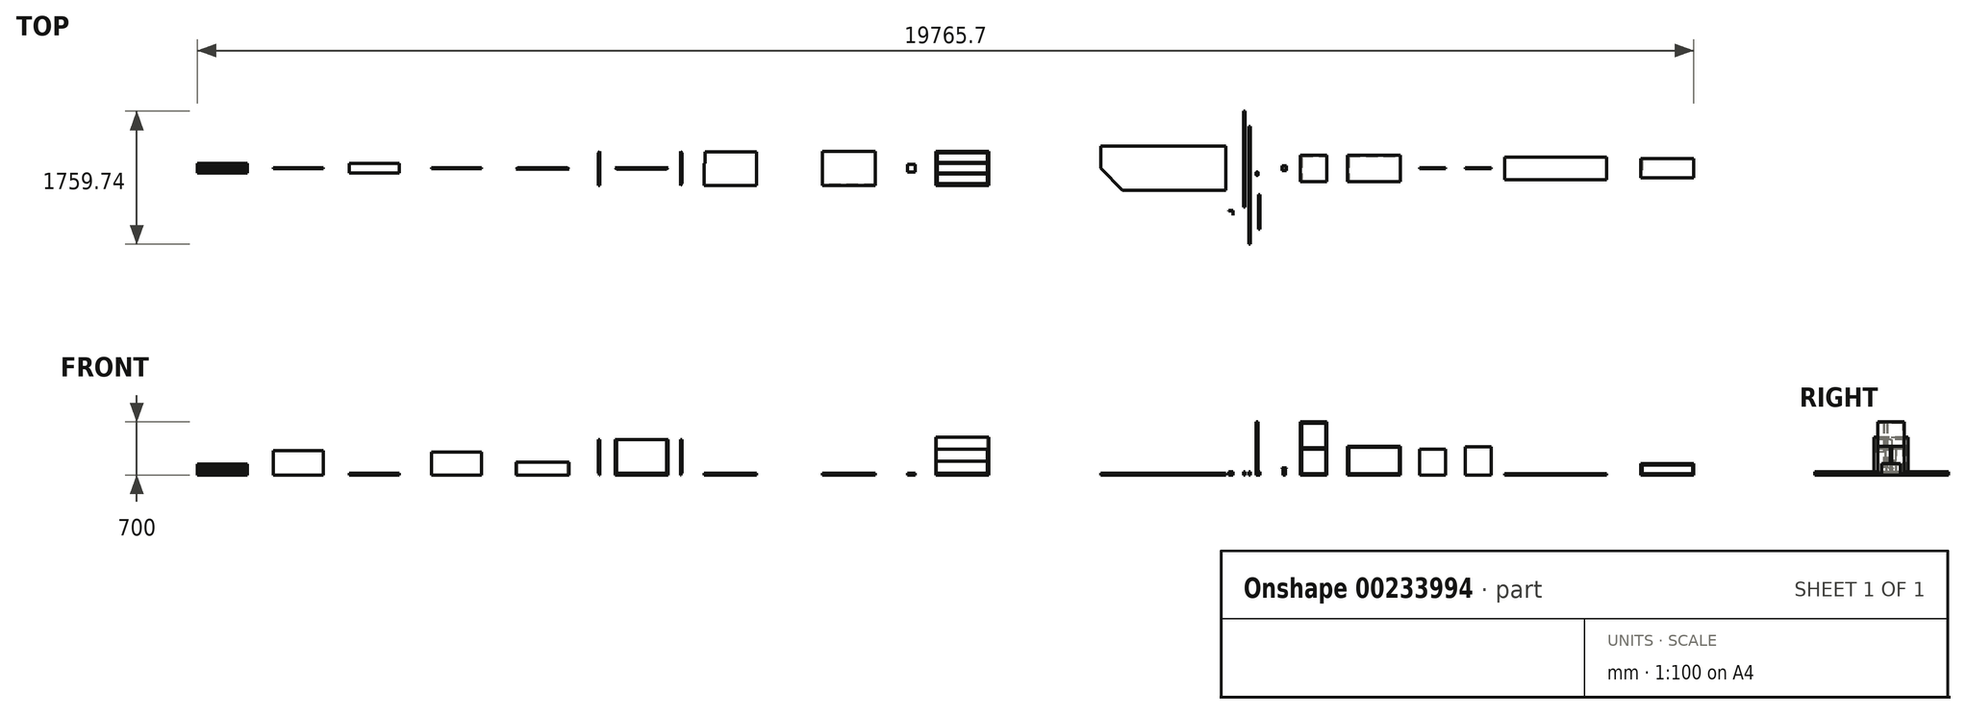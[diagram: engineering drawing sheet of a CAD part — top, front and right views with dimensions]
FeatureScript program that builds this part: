
annotation { "Feature Type Name" : "Feature", "Feature Type Description" : "" }
export const myFeature = defineFeature(function(context is Context, id is Id, definition is map)
    precondition{}
    {
        {
            var Q0;
            Q0=qCreatedBy(makeId("Top.planeOp"),FACE);
            var sketch = newSketch(context, id + "F0", { "sketchPlane" : qUnion([Q0])});
            skLineSegment(sketch, "E0.bottom", {"start": v(-825, -290) * mm, "end": v(825, -290) * mm});
            skLineSegment(sketch, "E0.top", {"start": v(-825, 290) * mm, "end": v(825, 290) * mm});
            skLineSegment(sketch, "E0.left", {"start": v(-825, -290) * mm, "end": v(-825, 290) * mm});
            skLineSegment(sketch, "E0.right", {"start": v(825, -290) * mm, "end": v(825, 290) * mm});
            skPoint(sketch, "E0.middle", {"position": v(0, 0) * mm});
            skSolve(sketch);
        }
        {
            var Q0;
            Q0 = qSketchRegion(id + "F0", true);
            extrude(context, id + "F1", {"entities" : qUnion([Q0]), "depth" : 21 * mm});
        }
        {
            var Q0;
            Q0=qCreatedBy(makeId("Top.planeOp"),FACE);
            var sketch = newSketch(context, id + "F2", { "sketchPlane" : qUnion([Q0])});
            skLineSegment(sketch, "E1.bottom", {"start": v(1133.64, 555.5) * mm, "end": v(1151.64, 555.5) * mm});
            skLineSegment(sketch, "E1.top", {"start": v(1133.64, -1004.5) * mm, "end": v(1151.64, -1004.5) * mm});
            skLineSegment(sketch, "E1.left", {"start": v(1133.64, 555.5) * mm, "end": v(1133.64, -1004.5) * mm});
            skLineSegment(sketch, "E1.right", {"start": v(1151.64, 555.5) * mm, "end": v(1151.64, -1004.5) * mm});
            skSolve(sketch);
        }
        {
            var Q0;
            Q0 = qSketchRegion(id + "F2", true);
            extrude(context, id + "F3", {"entities" : qUnion([Q0]), "depth" : 40 * mm});
        }
        {
            var Q0;
            Q0=qCreatedBy(makeId("Top.planeOp"),FACE);
            var sketch = newSketch(context, id + "F4", { "sketchPlane" : qUnion([Q0])});
            skLineSegment(sketch, "E2.bottom", {"start": v(1258.17, -803.03) * mm, "end": v(1276.17, -803.03) * mm});
            skLineSegment(sketch, "E2.top", {"start": v(1258.17, -351.03) * mm, "end": v(1276.17, -351.03) * mm});
            skLineSegment(sketch, "E2.left", {"start": v(1258.17, -803.03) * mm, "end": v(1258.17, -351.03) * mm});
            skLineSegment(sketch, "E2.right", {"start": v(1276.17, -803.03) * mm, "end": v(1276.17, -351.03) * mm});
            skSolve(sketch);
        }
        {
            var Q0;
            Q0 = qSketchRegion(id + "F4", true);
            extrude(context, id + "F5", {"entities" : qUnion([Q0]), "depth" : 40 * mm});
        }
        {
            var Q0;
            Q0=qCreatedBy(makeId("Top.planeOp"),FACE);
            var sketch = newSketch(context, id + "F6", { "sketchPlane" : qUnion([Q0])});
            skLineSegment(sketch, "E3", {"start": v(923.66, -561.71) * mm, "end": v(863.66, -561.71) * mm});
            skLineSegment(sketch, "E4", {"start": v(863.66, -561.71) * mm, "end": v(863.66, -559.71) * mm});
            skLineSegment(sketch, "E5", {"start": v(863.66, -559.71) * mm, "end": v(925.66, -559.71) * mm});
            skLineSegment(sketch, "E6", {"start": v(925.66, -559.71) * mm, "end": v(925.66, -621.71) * mm});
            skLineSegment(sketch, "E7", {"start": v(925.66, -621.71) * mm, "end": v(923.66, -621.71) * mm});
            skLineSegment(sketch, "E8", {"start": v(923.66, -621.71) * mm, "end": v(923.66, -561.71) * mm});
            skSolve(sketch);
        }
        {
            var Q0;
            Q0 = qSketchRegion(id + "F6", true);
            extrude(context, id + "F7", {"entities" : qUnion([Q0]), "depth" : 40 * mm});
        }
        {
            var Q0;
            Q0=qCreatedBy(makeId("Top.planeOp"),FACE);
            var sketch = newSketch(context, id + "F8", { "sketchPlane" : qUnion([Q0])});
            skLineSegment(sketch, "E9", {"start": v(1228.45, -53.77) * mm, "end": v(1228.45, -90.77) * mm});
            skArc(sketch, "E10", {"start": v(1256.45, -53.77) * mm, "mid": v(1242.45, -48.05) * mm, "end": v(1228.45, -53.77) * mm});
            skLineSegment(sketch, "E11", {"start": v(1256.45, -53.77) * mm, "end": v(1256.45, -90.77) * mm});
            skArc(sketch, "E12", {"start": v(1228.45, -90.77) * mm, "mid": v(1242.45, -96.48) * mm, "end": v(1256.45, -90.77) * mm});
            skSolve(sketch);
        }
        {
            var Q0;
            Q0 = qSketchRegion(id + "F8", true);
            extrude(context, id + "F9", {"entities" : qUnion([Q0]), "depth" : 700 * mm});
        }
        {
            var Q0;
            Q0=makeQuery(id+"F1.opExtrude","CAP_FACE",FACE,{"disambiguationData":[OSD([sQuery(id+"F0.wireOp",EDGE,"E0.bottom"),sQuery(id+"F0.wireOp",EDGE,"E0.top"),sQuery(id+"F0.wireOp",EDGE,"E0.left"),sQuery(id+"F0.wireOp",EDGE,"E0.right")])],"isStart":false});
            var sketch = newSketch(context, id + "F10", { "sketchPlane" : qUnion([Q0])});
            skLineSegment(sketch, "E13", {"start": v(-825, 0) * mm, "end": v(-535, -290) * mm});
            skLineSegment(sketch, "E14", {"start": v(-535, -290) * mm, "end": v(-825, -290) * mm});
            skLineSegment(sketch, "E15", {"start": v(-825, -290) * mm, "end": v(-825, 0) * mm});
            skSolve(sketch);
        }
        {
            var Q0;
            Q0 = qSketchRegion(id + "F10", true);
            extrude(context, id + "F11", {"entities" : qUnion([Q0]), "operationType" : NewBodyOperationType.REMOVE, "endBound" : BoundingType.UP_TO_NEXT, "oppositeDirection" : true, "depth" : 25 * mm});
        }
        {
            var Q0;
            Q0=qCreatedBy(makeId("Top.planeOp"),FACE);
            var sketch = newSketch(context, id + "F12", { "sketchPlane" : qUnion([Q0])});
            skLineSegment(sketch, "E16", {"start": v(1082.97, 755.24) * mm, "end": v(1064.97, 755.24) * mm});
            skLineSegment(sketch, "E17", {"start": v(1064.97, 755.24) * mm, "end": v(1064.97, -514.76) * mm});
            skLineSegment(sketch, "E18", {"start": v(1064.97, -514.76) * mm, "end": v(1082.97, -514.76) * mm});
            skLineSegment(sketch, "E19", {"start": v(1082.97, -514.76) * mm, "end": v(1082.97, 755.24) * mm});
            skSolve(sketch);
        }
        {
            var Q0;
            Q0 = qSketchRegion(id + "F12", true);
            extrude(context, id + "F13", {"entities" : qUnion([Q0]), "depth" : 40 * mm});
        }
        {
            var Q0;
            Q0=qCreatedBy(makeId("Top.planeOp"),FACE);
            var sketch = newSketch(context, id + "F14", { "sketchPlane" : qUnion([Q0])});
            skLineSegment(sketch, "E20.bottom", {"start": v(1813.46, -175) * mm, "end": v(2163.46, -175) * mm});
            skLineSegment(sketch, "E20.top", {"start": v(1813.46, 175) * mm, "end": v(2163.46, 175) * mm});
            skLineSegment(sketch, "E20.left", {"start": v(1813.46, -175) * mm, "end": v(1813.46, 175) * mm});
            skLineSegment(sketch, "E20.right", {"start": v(2163.46, -175) * mm, "end": v(2163.46, 175) * mm});
            skPoint(sketch, "E20.middle", {"position": v(1988.46, 0) * mm});
            skSolve(sketch);
        }
        {
            var Q0;
            Q0 = qSketchRegion(id + "F14", true);
            extrude(context, id + "F15", {"entities" : qUnion([Q0]), "depth" : 700 * mm});
        }
        {
            var Q0;
            Q0=makeQuery(id+"F15.opExtrude","SWEPT_FACE",FACE,{"disambiguationData":[OSD([sQuery(id+"F14.wireOp",EDGE,"E20.bottom")])]});
            var sketch = newSketch(context, id + "F16", { "sketchPlane" : qUnion([Q0])});
            skLineSegment(sketch, "E21.bottom", {"start": v(1829.46, 358) * mm, "end": v(2147.46, 358) * mm});
            skLineSegment(sketch, "E21.top", {"start": v(1829.46, 684) * mm, "end": v(2147.46, 684) * mm});
            skLineSegment(sketch, "E21.left", {"start": v(1829.46, 358) * mm, "end": v(1829.46, 684) * mm});
            skLineSegment(sketch, "E21.right", {"start": v(2147.46, 358) * mm, "end": v(2147.46, 684) * mm});
            skPoint(sketch, "E21.middle", {"position": v(1988.46, 521) * mm});
            skPoint(sketch, "E21.middle.positionSnap0", {"position": v(1988.46, 700) * mm});
            skPoint(sketch, "E21.centerSnap0", {"position": v(1988.46, 700) * mm});
            skLineSegment(sketch, "E22.bottom", {"start": v(1829.46, 16) * mm, "end": v(2147.46, 16) * mm});
            skLineSegment(sketch, "E22.top", {"start": v(1829.46, 342) * mm, "end": v(2147.46, 342) * mm});
            skLineSegment(sketch, "E22.left", {"start": v(1829.46, 16) * mm, "end": v(1829.46, 342) * mm});
            skLineSegment(sketch, "E22.right", {"start": v(2147.46, 16) * mm, "end": v(2147.46, 342) * mm});
            skPoint(sketch, "E22.middle", {"position": v(1988.46, 179) * mm});
            skSolve(sketch);
        }
        {
            var Q0;
            Q0 = qSketchRegion(id + "F16", true);
            extrude(context, id + "F17", {"entities" : qUnion([Q0]), "operationType" : NewBodyOperationType.REMOVE, "oppositeDirection" : true, "depth" : 334 * mm});
        }
        {
            var Q0;
            Q0=qCreatedBy(makeId("Top.planeOp"),FACE);
            var sketch = newSketch(context, id + "F18", { "sketchPlane" : qUnion([Q0])});
            skLineSegment(sketch, "E23.bottom", {"start": v(2436.18, -175) * mm, "end": v(3136.18, -175) * mm});
            skLineSegment(sketch, "E23.top", {"start": v(2436.18, 175) * mm, "end": v(3136.18, 175) * mm});
            skLineSegment(sketch, "E23.left", {"start": v(2436.18, -175) * mm, "end": v(2436.18, 175) * mm});
            skLineSegment(sketch, "E23.right", {"start": v(3136.18, -175) * mm, "end": v(3136.18, 175) * mm});
            skPoint(sketch, "E23.middle", {"position": v(2786.18, 0) * mm});
            skSolve(sketch);
        }
        {
            var Q0;
            Q0 = qSketchRegion(id + "F18", true);
            extrude(context, id + "F19", {"entities" : qUnion([Q0]), "depth" : 380 * mm});
        }
        {
            var Q0;
            Q0=makeQuery(id+"F19.opExtrude","SWEPT_FACE",FACE,{"disambiguationData":[OSD([sQuery(id+"F18.wireOp",EDGE,"E23.bottom")])]});
            var sketch = newSketch(context, id + "F20", { "sketchPlane" : qUnion([Q0])});
            skLineSegment(sketch, "E24.bottom", {"start": v(2452.18, 16) * mm, "end": v(3120.18, 16) * mm});
            skLineSegment(sketch, "E24.top", {"start": v(2452.18, 364) * mm, "end": v(3120.18, 364) * mm});
            skLineSegment(sketch, "E24.left", {"start": v(2452.18, 16) * mm, "end": v(2452.18, 364) * mm});
            skLineSegment(sketch, "E24.right", {"start": v(3120.18, 16) * mm, "end": v(3120.18, 364) * mm});
            skPoint(sketch, "E24.middle", {"position": v(2786.18, 190) * mm});
            skPoint(sketch, "E24.middle.positionSnap0", {"position": v(2436.18, 190) * mm});
            skPoint(sketch, "E24.centerSnap0", {"position": v(2436.18, 190) * mm});
            skSolve(sketch);
        }
        {
            var Q0;
            Q0 = qSketchRegion(id + "F20", true);
            extrude(context, id + "F21", {"entities" : qUnion([Q0]), "operationType" : NewBodyOperationType.REMOVE, "oppositeDirection" : true, "depth" : 334 * mm});
        }
        {
            var Q0;
            Q0=qCreatedBy(makeId("Top.planeOp"),FACE);
            var sketch = newSketch(context, id + "F22", { "sketchPlane" : qUnion([Q0])});
            skLineSegment(sketch, "E25.bottom", {"start": v(3728.23, -8) * mm, "end": v(3388.23, -8) * mm});
            skLineSegment(sketch, "E25.top", {"start": v(3728.23, 8) * mm, "end": v(3388.23, 8) * mm});
            skLineSegment(sketch, "E25.left", {"start": v(3728.23, -8) * mm, "end": v(3728.23, 8) * mm});
            skLineSegment(sketch, "E25.right", {"start": v(3388.23, -8) * mm, "end": v(3388.23, 8) * mm});
            skPoint(sketch, "E25.middle", {"position": v(3558.23, 0) * mm});
            skSolve(sketch);
        }
        {
            var Q0;
            Q0 = qSketchRegion(id + "F22", true);
            extrude(context, id + "F23", {"entities" : qUnion([Q0]), "depth" : 340 * mm});
        }
        {
            var Q0;
            Q0=qCreatedBy(makeId("Top.planeOp"),FACE);
            var sketch = newSketch(context, id + "F24", { "sketchPlane" : qUnion([Q0])});
            skLineSegment(sketch, "E26.bottom", {"start": v(3990.26, -8) * mm, "end": v(4330.26, -8) * mm});
            skLineSegment(sketch, "E26.top", {"start": v(3990.26, 8) * mm, "end": v(4330.26, 8) * mm});
            skLineSegment(sketch, "E26.left", {"start": v(3990.26, -8) * mm, "end": v(3990.26, 8) * mm});
            skLineSegment(sketch, "E26.right", {"start": v(4330.26, -8) * mm, "end": v(4330.26, 8) * mm});
            skPoint(sketch, "E26.middle", {"position": v(4160.26, 0) * mm});
            skSolve(sketch);
        }
        {
            var Q0;
            Q0 = qSketchRegion(id + "F24", true);
            extrude(context, id + "F25", {"entities" : qUnion([Q0]), "depth" : 370 * mm});
        }
        {
            var Q0;
            Q0=qCreatedBy(makeId("Top.planeOp"),FACE);
            var sketch = newSketch(context, id + "F26", { "sketchPlane" : qUnion([Q0])});
            skLineSegment(sketch, "E27.bottom", {"start": v(4509.18, -150) * mm, "end": v(5859.18, -150) * mm});
            skLineSegment(sketch, "E27.top", {"start": v(4509.18, 150) * mm, "end": v(5859.18, 150) * mm});
            skLineSegment(sketch, "E27.left", {"start": v(4509.18, -150) * mm, "end": v(4509.18, 150) * mm});
            skLineSegment(sketch, "E27.right", {"start": v(5859.18, -150) * mm, "end": v(5859.18, 150) * mm});
            skPoint(sketch, "E27.middle", {"position": v(5184.18, 0) * mm});
            skSolve(sketch);
        }
        {
            var Q0;
            Q0 = qSketchRegion(id + "F26", true);
            extrude(context, id + "F27", {"entities" : qUnion([Q0]), "depth" : 16 * mm});
        }
        {
            var Q0;
            Q0=qCreatedBy(makeId("Top.planeOp"),FACE);
            var sketch = newSketch(context, id + "F28", { "sketchPlane" : qUnion([Q0])});
            skLineSegment(sketch, "E28.bottom", {"start": v(1570, -30) * mm, "end": v(1630, -30) * mm});
            skLineSegment(sketch, "E28.top", {"start": v(1570, 30) * mm, "end": v(1630, 30) * mm});
            skLineSegment(sketch, "E28.left", {"start": v(1570, -30) * mm, "end": v(1570, 30) * mm});
            skLineSegment(sketch, "E28.right", {"start": v(1630, -30) * mm, "end": v(1630, 30) * mm});
            skPoint(sketch, "E28.middle", {"position": v(1600, 0) * mm});
            skSolve(sketch);
        }
        {
            var Q0;
            Q0 = qSketchRegion(id + "F28", true);
            extrude(context, id + "F29", {"entities" : qUnion([Q0]), "depth" : 90 * mm});
        }
        {
            var Q0;
            Q0=qCreatedBy(makeId("Front.planeOp"),FACE);
            var sketch = newSketch(context, id + "F30", { "sketchPlane" : qUnion([Q0])});
            skLineSegment(sketch, "E29", {"start": v(1600, 158.23) * mm, "end": v(1600, -41.77) * mm, "construction": true});
            skSolve(sketch);
        }
        {
            var Q0;
            Q0=qCreatedBy(makeId("Front.planeOp"),FACE);
            var sketch = newSketch(context, id + "F31", { "sketchPlane" : qUnion([Q0])});
            skLineSegment(sketch, "E30", {"start": v(1615, 0) * mm, "end": v(1615, 83) * mm});
            skLineSegment(sketch, "E31", {"start": v(1630, 85) * mm, "end": v(1620, 85) * mm});
            skLineSegment(sketch, "E32", {"start": v(1620, 85) * mm, "end": v(1615, 83) * mm});
            skLineSegment(sketch, "E33", {"start": v(1615, 0) * mm, "end": v(1649.67, 0) * mm});
            skLineSegment(sketch, "E34", {"start": v(1649.67, 0) * mm, "end": v(1649.67, 85) * mm});
            skLineSegment(sketch, "E35", {"start": v(1649.67, 85) * mm, "end": v(1630, 85) * mm});
            skSolve(sketch);
        }
        {
            var Q0;
            Q0 = qSketchRegion(id + "F31", true);
            var Q1;
            Q1=sQuery(id+"F30.wireOp",EDGE,"E29");
            revolve(context, id + "F32", {"operationType" : NewBodyOperationType.REMOVE, "entities" : qUnion([Q0]), "axis" : qUnion([Q1]), "revolveType" : RevolveType.FULL, "oppositeDirection" : true});
        }
        {
            var Q0;
            Q0=qCreatedBy(makeId("Top.planeOp"),FACE);
            var sketch = newSketch(context, id + "F33", { "sketchPlane" : qUnion([Q0])});
            skLineSegment(sketch, "E36.bottom", {"start": v(6310, -125) * mm, "end": v(7010, -125) * mm});
            skLineSegment(sketch, "E36.top", {"start": v(6310, 125) * mm, "end": v(7010, 125) * mm});
            skLineSegment(sketch, "E36.left", {"start": v(6310, -125) * mm, "end": v(6310, 125) * mm});
            skLineSegment(sketch, "E36.right", {"start": v(7010, -125) * mm, "end": v(7010, 125) * mm});
            skPoint(sketch, "E36.middle", {"position": v(6660, 0) * mm});
            skSolve(sketch);
        }
        {
            var Q0;
            Q0 = qSketchRegion(id + "F33", true);
            extrude(context, id + "F34", {"entities" : qUnion([Q0]), "depth" : 150 * mm});
        }
        {
            var Q0;
            Q0=makeQuery(id+"F34.opExtrude","SWEPT_FACE",FACE,{"disambiguationData":[OSD([sQuery(id+"F33.wireOp",EDGE,"E36.bottom")])]});
            var sketch = newSketch(context, id + "F35", { "sketchPlane" : qUnion([Q0])});
            skLineSegment(sketch, "E37.bottom", {"start": v(6326, 16) * mm, "end": v(6994, 16) * mm});
            skLineSegment(sketch, "E37.top", {"start": v(6326, 134) * mm, "end": v(6994, 134) * mm});
            skLineSegment(sketch, "E37.left", {"start": v(6326, 16) * mm, "end": v(6326, 134) * mm});
            skLineSegment(sketch, "E37.right", {"start": v(6994, 16) * mm, "end": v(6994, 134) * mm});
            skPoint(sketch, "E37.middle", {"position": v(6660, 75) * mm});
            skPoint(sketch, "E37.middle.positionSnap0", {"position": v(6660, 150) * mm});
            skPoint(sketch, "E37.centerSnap0", {"position": v(6660, 150) * mm});
            skSolve(sketch);
        }
        {
            var Q0;
            Q0 = qSketchRegion(id + "F35", true);
            extrude(context, id + "F36", {"entities" : qUnion([Q0]), "operationType" : NewBodyOperationType.REMOVE, "oppositeDirection" : true, "depth" : 334 * mm});
        }
        {
            var Q0;
            Q0=qCreatedBy(makeId("Top.planeOp"),FACE);
            var sketch = newSketch(context, id + "F37", { "sketchPlane" : qUnion([Q0])});
            skLineSegment(sketch, "E38.bottom", {"start": v(-3001.17, -225) * mm, "end": v(-2301.17, -225) * mm});
            skLineSegment(sketch, "E38.top", {"start": v(-3001.17, 225) * mm, "end": v(-2301.17, 225) * mm});
            skLineSegment(sketch, "E38.left", {"start": v(-3001.17, -225) * mm, "end": v(-3001.17, 225) * mm});
            skLineSegment(sketch, "E38.right", {"start": v(-2301.17, -225) * mm, "end": v(-2301.17, 225) * mm});
            skPoint(sketch, "E38.middle", {"position": v(-2651.17, 0) * mm});
            skSolve(sketch);
        }
        {
            var Q0;
            Q0=makeQuery(id+"F37.imprint","IMPRINT",FACE,{"disambiguationData":[TD([[makeQuery(id+"F37.imprint","IMPRINT",EDGE,{"derivedFrom":sQuery(id+"F37.wireOp",EDGE,"E38.bottom")}),1.0]])]});
            extrude(context, id + "F38", {"entities" : qUnion([Q0]), "depth" : 500 * mm});
        }
        {
            var Q0;
            Q0=makeQuery(id+"F38.opExtrude","SWEPT_FACE",FACE,{"disambiguationData":[OSD([sQuery(id+"F37.wireOp",EDGE,"E38.left")])]});
            var sketch = newSketch(context, id + "F39", { "sketchPlane" : qUnion([Q0])});
            skLineSegment(sketch, "E39", {"start": v(225, 20) * mm, "end": v(-65, 20) * mm});
            skLineSegment(sketch, "E40", {"start": v(-65, 20) * mm, "end": v(-65, 180) * mm});
            skLineSegment(sketch, "E41", {"start": v(-65, 180) * mm, "end": v(75, 180) * mm});
            skLineSegment(sketch, "E42", {"start": v(75, 180) * mm, "end": v(75, 340) * mm});
            skLineSegment(sketch, "E43", {"start": v(75, 340) * mm, "end": v(225, 340) * mm});
            skLineSegment(sketch, "E44", {"start": v(225, 340) * mm, "end": v(225, 20) * mm});
            skSolve(sketch);
        }
        {
            var Q0;
            Q0 = qSketchRegion(id + "F39", true);
            extrude(context, id + "F40", {"entities" : qUnion([Q0]), "operationType" : NewBodyOperationType.REMOVE, "oppositeDirection" : true, "depth" : 680 * mm});
        }
        {
            var Q0;
            Q0=makeQuery(id+"F38.opExtrude","CAP_FACE",FACE,{"disambiguationData":[OSD([sQuery(id+"F37.wireOp",EDGE,"E38.bottom"),sQuery(id+"F37.wireOp",EDGE,"E38.top"),sQuery(id+"F37.wireOp",EDGE,"E38.left"),sQuery(id+"F37.wireOp",EDGE,"E38.right")])],"isStart":false});
            var sketch = newSketch(context, id + "F41", { "sketchPlane" : qUnion([Q0])});
            skLineSegment(sketch, "E45.bottom", {"start": v(-2981.17, 205) * mm, "end": v(-2321.17, 205) * mm});
            skLineSegment(sketch, "E45.top", {"start": v(-2981.17, 75) * mm, "end": v(-2321.17, 75) * mm});
            skLineSegment(sketch, "E45.left", {"start": v(-2981.17, 205) * mm, "end": v(-2981.17, 75) * mm});
            skLineSegment(sketch, "E45.right", {"start": v(-2321.17, 205) * mm, "end": v(-2321.17, 75) * mm});
            skSolve(sketch);
        }
        {
            var Q0;
            Q0 = qSketchRegion(id + "F41", true);
            extrude(context, id + "F42", {"entities" : qUnion([Q0]), "operationType" : NewBodyOperationType.REMOVE, "oppositeDirection" : true, "depth" : 480 * mm});
        }
        {
            var Q0;
            Q0=makeQuery(id+"F38.opExtrude","CAP_FACE",FACE,{"disambiguationData":[OSD([sQuery(id+"F37.wireOp",EDGE,"E38.bottom"),sQuery(id+"F37.wireOp",EDGE,"E38.top"),sQuery(id+"F37.wireOp",EDGE,"E38.left"),sQuery(id+"F37.wireOp",EDGE,"E38.right")])],"isStart":false});
            var sketch = newSketch(context, id + "F43", { "sketchPlane" : qUnion([Q0])});
            skLineSegment(sketch, "E46.bottom", {"start": v(-2981.17, 65) * mm, "end": v(-2321.17, 65) * mm});
            skLineSegment(sketch, "E46.top", {"start": v(-2981.17, -65) * mm, "end": v(-2321.17, -65) * mm});
            skLineSegment(sketch, "E46.left", {"start": v(-2981.17, 65) * mm, "end": v(-2981.17, -65) * mm});
            skLineSegment(sketch, "E46.right", {"start": v(-2321.17, 65) * mm, "end": v(-2321.17, -65) * mm});
            skSolve(sketch);
        }
        {
            var Q0;
            Q0 = qSketchRegion(id + "F43", true);
            extrude(context, id + "F44", {"entities" : qUnion([Q0]), "operationType" : NewBodyOperationType.REMOVE, "oppositeDirection" : true, "depth" : 310 * mm});
        }
        {
            var Q0;
            Q0=makeQuery(id+"F38.opExtrude","CAP_FACE",FACE,{"disambiguationData":[OSD([sQuery(id+"F37.wireOp",EDGE,"E38.bottom"),sQuery(id+"F37.wireOp",EDGE,"E38.top"),sQuery(id+"F37.wireOp",EDGE,"E38.left"),sQuery(id+"F37.wireOp",EDGE,"E38.right")])],"isStart":false});
            var sketch = newSketch(context, id + "F45", { "sketchPlane" : qUnion([Q0])});
            skLineSegment(sketch, "E47.bottom", {"start": v(-2981.17, -75) * mm, "end": v(-2321.17, -75) * mm});
            skLineSegment(sketch, "E47.top", {"start": v(-2981.17, -205) * mm, "end": v(-2321.17, -205) * mm});
            skLineSegment(sketch, "E47.left", {"start": v(-2981.17, -75) * mm, "end": v(-2981.17, -205) * mm});
            skLineSegment(sketch, "E47.right", {"start": v(-2321.17, -75) * mm, "end": v(-2321.17, -205) * mm});
            skSolve(sketch);
        }
        {
            var Q0;
            Q0 = qSketchRegion(id + "F45", true);
            extrude(context, id + "F46", {"entities" : qUnion([Q0]), "operationType" : NewBodyOperationType.REMOVE, "oppositeDirection" : true, "depth" : 150 * mm});
        }
        {
            var Q0;
            Q0=makeQuery(id+"F38.opExtrude","CAP_FACE",FACE,{"disambiguationData":[OSD([sQuery(id+"F37.wireOp",EDGE,"E38.bottom"),sQuery(id+"F37.wireOp",EDGE,"E38.top"),sQuery(id+"F37.wireOp",EDGE,"E38.left"),sQuery(id+"F37.wireOp",EDGE,"E38.right")])],"isStart":false});
            var sketch = newSketch(context, id + "F47", { "sketchPlane" : qUnion([Q0])});
            skLineSegment(sketch, "E48.bottom", {"start": v(-2981.17, 75) * mm, "end": v(-2321.17, 75) * mm});
            skLineSegment(sketch, "E48.top", {"start": v(-2981.17, 65) * mm, "end": v(-2321.17, 65) * mm});
            skLineSegment(sketch, "E48.left", {"start": v(-2981.17, 75) * mm, "end": v(-2981.17, 65) * mm});
            skLineSegment(sketch, "E48.right", {"start": v(-2321.17, 75) * mm, "end": v(-2321.17, 65) * mm});
            skSolve(sketch);
        }
        {
            var Q0;
            Q0 = qSketchRegion(id + "F47", true);
            extrude(context, id + "F48", {"entities" : qUnion([Q0]), "operationType" : NewBodyOperationType.REMOVE, "oppositeDirection" : true, "depth" : 150 * mm});
        }
        {
            var Q0;
            Q0=qCreatedBy(makeId("Top.planeOp"),FACE);
            var sketch = newSketch(context, id + "F49", { "sketchPlane" : qUnion([Q0])});
            skLineSegment(sketch, "E49.bottom", {"start": v(-3373.28, -50) * mm, "end": v(-3273.28, -50) * mm});
            skLineSegment(sketch, "E49.top", {"start": v(-3373.28, 50) * mm, "end": v(-3273.28, 50) * mm});
            skLineSegment(sketch, "E49.left", {"start": v(-3373.28, -50) * mm, "end": v(-3373.28, 50) * mm});
            skLineSegment(sketch, "E49.right", {"start": v(-3273.28, -50) * mm, "end": v(-3273.28, 50) * mm});
            skPoint(sketch, "E49.middle", {"position": v(-3323.28, 0) * mm});
            skSolve(sketch);
        }
        {
            var Q0;
            Q0 = qSketchRegion(id + "F49", true);
            extrude(context, id + "F50", {"entities" : qUnion([Q0]), "depth" : 20 * mm});
        }
        {
            var Q0;
            Q0=qCreatedBy(makeId("Top.planeOp"),FACE);
            var sketch = newSketch(context, id + "F51", { "sketchPlane" : qUnion([Q0])});
            skLineSegment(sketch, "E50.bottom", {"start": v(-4499.44, -225) * mm, "end": v(-3799.44, -225) * mm});
            skLineSegment(sketch, "E50.top", {"start": v(-4499.44, 225) * mm, "end": v(-3799.44, 225) * mm});
            skLineSegment(sketch, "E50.left", {"start": v(-4499.44, -225) * mm, "end": v(-4499.44, 225) * mm});
            skLineSegment(sketch, "E50.right", {"start": v(-3799.44, -225) * mm, "end": v(-3799.44, 225) * mm});
            skPoint(sketch, "E50.middle", {"position": v(-4149.44, 0) * mm});
            skSolve(sketch);
        }
        {
            var Q0;
            Q0=makeQuery(id+"F51.imprint","IMPRINT",FACE,{"disambiguationData":[TD([[makeQuery(id+"F51.imprint","IMPRINT",EDGE,{"derivedFrom":sQuery(id+"F51.wireOp",EDGE,"E50.bottom")}),1.0]])]});
            extrude(context, id + "F52", {"entities" : qUnion([Q0]), "depth" : 20 * mm});
        }
        {
            var Q0;
            Q0=makeQuery(id+"F52.opExtrude","SWEPT_FACE",FACE,{"disambiguationData":[OSD([sQuery(id+"F51.wireOp",EDGE,"E50.left")])]});
            var sketch = newSketch(context, id + "F53", { "sketchPlane" : qUnion([Q0])});
            skLineSegment(sketch, "E51", {"start": v(225, 10) * mm, "end": v(215, 0) * mm});
            skLineSegment(sketch, "E52", {"start": v(215, 0) * mm, "end": v(225, 0) * mm});
            skLineSegment(sketch, "E53", {"start": v(225, 0) * mm, "end": v(225, 10) * mm});
            skSolve(sketch);
        }
        {
            var Q0;
            Q0 = qSketchRegion(id + "F53", true);
            extrude(context, id + "F54", {"entities" : qUnion([Q0]), "operationType" : NewBodyOperationType.REMOVE, "oppositeDirection" : true, "depth" : 700 * mm});
        }
        {
            var Q0;
            Q0=qCreatedBy(makeId("Top.planeOp"),FACE);
            var sketch = newSketch(context, id + "F55", { "sketchPlane" : qUnion([Q0])});
            skLineSegment(sketch, "E54.bottom", {"start": v(-6060.66, -225) * mm, "end": v(-5360.66, -225) * mm});
            skLineSegment(sketch, "E54.top", {"start": v(-6060.66, 225) * mm, "end": v(-5360.66, 225) * mm});
            skLineSegment(sketch, "E54.left", {"start": v(-6060.66, -225) * mm, "end": v(-6060.66, 225) * mm});
            skLineSegment(sketch, "E54.right", {"start": v(-5360.66, -225) * mm, "end": v(-5360.66, 225) * mm});
            skPoint(sketch, "E54.middle", {"position": v(-5710.66, 0) * mm});
            skSolve(sketch);
        }
        {
            var Q0;
            Q0 = qSketchRegion(id + "F55", true);
            extrude(context, id + "F56", {"entities" : qUnion([Q0]), "depth" : 20 * mm});
        }
        {
            var Q0;
            Q0=makeQuery(id+"F56.opExtrude","CAP_FACE",FACE,{"disambiguationData":[OSD([sQuery(id+"F55.wireOp",EDGE,"E54.bottom"),sQuery(id+"F55.wireOp",EDGE,"E54.top"),sQuery(id+"F55.wireOp",EDGE,"E54.left"),sQuery(id+"F55.wireOp",EDGE,"E54.right")])],"isStart":false});
            var sketch = newSketch(context, id + "F57", { "sketchPlane" : qUnion([Q0])});
            skLineSegment(sketch, "E55", {"start": v(-6060.66, 65) * mm, "end": v(-6050.66, 65) * mm});
            skLineSegment(sketch, "E56", {"start": v(-6050.66, 65) * mm, "end": v(-6050.66, 215) * mm});
            skLineSegment(sketch, "E57", {"start": v(-6050.66, 215) * mm, "end": v(-5370.66, 215) * mm});
            skLineSegment(sketch, "E58", {"start": v(-5370.66, 215) * mm, "end": v(-5370.66, -225) * mm});
            skLineSegment(sketch, "E59", {"start": v(-5370.66, -225) * mm, "end": v(-5360.66, -225) * mm});
            skLineSegment(sketch, "E60", {"start": v(-5360.66, -225) * mm, "end": v(-5360.66, 225) * mm});
            skLineSegment(sketch, "E61", {"start": v(-5360.66, 225) * mm, "end": v(-6060.66, 225) * mm});
            skLineSegment(sketch, "E62", {"start": v(-6060.66, 225) * mm, "end": v(-6060.66, 65) * mm});
            skSolve(sketch);
        }
        {
            var Q0;
            Q0 = qSketchRegion(id + "F57", true);
            extrude(context, id + "F58", {"entities" : qUnion([Q0]), "operationType" : NewBodyOperationType.REMOVE, "oppositeDirection" : true, "depth" : 20 * mm});
        }
        {
            var Q0;
            Q0=qCreatedBy(makeId("Top.planeOp"),FACE);
            var sketch = newSketch(context, id + "F59", { "sketchPlane" : qUnion([Q0])});
            skLineSegment(sketch, "E63.bottom", {"start": v(-6353.68, 225) * mm, "end": v(-6373.68, 225) * mm});
            skLineSegment(sketch, "E63.top", {"start": v(-6353.68, -225) * mm, "end": v(-6373.68, -225) * mm});
            skLineSegment(sketch, "E63.left", {"start": v(-6353.68, 225) * mm, "end": v(-6353.68, -225) * mm});
            skLineSegment(sketch, "E63.right", {"start": v(-6373.68, 225) * mm, "end": v(-6373.68, -225) * mm});
            skPoint(sketch, "E63.middle", {"position": v(-6363.68, 0) * mm});
            skSolve(sketch);
        }
        {
            var Q0;
            Q0 = qSketchRegion(id + "F59", true);
            extrude(context, id + "F60", {"entities" : qUnion([Q0]), "depth" : 470 * mm});
        }
        {
            var Q0;
            Q0=makeQuery(id+"F60.opExtrude","CAP_FACE",FACE,{"disambiguationData":[OSD([sQuery(id+"F59.wireOp",EDGE,"E63.bottom"),sQuery(id+"F59.wireOp",EDGE,"E63.top"),sQuery(id+"F59.wireOp",EDGE,"E63.left"),sQuery(id+"F59.wireOp",EDGE,"E63.right")])],"isStart":false});
            var sketch = newSketch(context, id + "F61", { "sketchPlane" : qUnion([Q0])});
            skLineSegment(sketch, "E64", {"start": v(-6373.68, 225) * mm, "end": v(-6353.68, 225) * mm});
            skLineSegment(sketch, "E65", {"start": v(-6353.68, 225) * mm, "end": v(-6353.68, 205) * mm});
            skLineSegment(sketch, "E66", {"start": v(-6353.68, 205) * mm, "end": v(-6373.68, 225) * mm});
            skSolve(sketch);
        }
        {
            var Q0;
            Q0 = qSketchRegion(id + "F61", true);
            extrude(context, id + "F62", {"entities" : qUnion([Q0]), "operationType" : NewBodyOperationType.REMOVE, "oppositeDirection" : true, "depth" : 470 * mm});
        }
        {
            var Q0;
            Q0=makeQuery(id+"F60.opExtrude","SWEPT_FACE",FACE,{"disambiguationData":[OSD([sQuery(id+"F59.wireOp",EDGE,"E63.top")])]});
            var sketch = newSketch(context, id + "F63", { "sketchPlane" : qUnion([Q0])});
            skLineSegment(sketch, "E67.bottom", {"start": v(-6353.68, 0) * mm, "end": v(-6363.68, 0) * mm});
            skLineSegment(sketch, "E67.top", {"start": v(-6353.68, 20) * mm, "end": v(-6363.68, 20) * mm});
            skLineSegment(sketch, "E67.left", {"start": v(-6353.68, 0) * mm, "end": v(-6353.68, 20) * mm});
            skLineSegment(sketch, "E67.right", {"start": v(-6363.68, 0) * mm, "end": v(-6363.68, 20) * mm});
            skSolve(sketch);
        }
        {
            var Q0;
            Q0 = qSketchRegion(id + "F63", true);
            extrude(context, id + "F64", {"entities" : qUnion([Q0]), "operationType" : NewBodyOperationType.REMOVE, "oppositeDirection" : true, "depth" : 470 * mm});
        }
        {
            var Q0;
            Q0=makeQuery(id+"F60.opExtrude","SWEPT_FACE",FACE,{"disambiguationData":[OSD([sQuery(id+"F59.wireOp",EDGE,"E63.right")])]});
            var sketch = newSketch(context, id + "F65", { "sketchPlane" : qUnion([Q0])});
            skLineSegment(sketch, "E68", {"start": v(225, 0) * mm, "end": v(-65, 0) * mm});
            skLineSegment(sketch, "E69", {"start": v(-65, 0) * mm, "end": v(-65, 150) * mm});
            skLineSegment(sketch, "E70", {"start": v(-65, 150) * mm, "end": v(75, 150) * mm});
            skLineSegment(sketch, "E71", {"start": v(75, 150) * mm, "end": v(75, 300) * mm});
            skLineSegment(sketch, "E72", {"start": v(75, 300) * mm, "end": v(225, 300) * mm});
            skLineSegment(sketch, "E73", {"start": v(225, 300) * mm, "end": v(225, 0) * mm});
            skSolve(sketch);
        }
        {
            var Q0;
            Q0 = qSketchRegion(id + "F65", true);
            extrude(context, id + "F66", {"entities" : qUnion([Q0]), "operationType" : NewBodyOperationType.REMOVE, "oppositeDirection" : true, "depth" : 20 * mm});
        }
        {
            var Q0;
            Q0=makeQuery(id+"F60.opExtrude","CAP_FACE",FACE,{"disambiguationData":[OSD([sQuery(id+"F59.wireOp",EDGE,"E63.bottom"),sQuery(id+"F59.wireOp",EDGE,"E63.top"),sQuery(id+"F59.wireOp",EDGE,"E63.left"),sQuery(id+"F59.wireOp",EDGE,"E63.right")])],"isStart":false});
            var sketch = newSketch(context, id + "F67", { "sketchPlane" : qUnion([Q0])});
            skLineSegment(sketch, "E74", {"start": v(-6373.68, -225) * mm, "end": v(-6353.68, -225) * mm});
            skLineSegment(sketch, "E75", {"start": v(-6353.68, -225) * mm, "end": v(-6353.68, -205) * mm});
            skLineSegment(sketch, "E76", {"start": v(-6353.68, -205) * mm, "end": v(-6373.68, -225) * mm});
            skSolve(sketch);
        }
        {
            var Q0;
            Q0 = qSketchRegion(id + "F67", true);
            extrude(context, id + "F68", {"entities" : qUnion([Q0]), "operationType" : NewBodyOperationType.REMOVE, "oppositeDirection" : true, "depth" : 470 * mm});
        }
        {
            var Q0;
            Q0=qCreatedBy(makeId("Top.planeOp"),FACE);
            var sketch = newSketch(context, id + "F69", { "sketchPlane" : qUnion([Q0])});
            skLineSegment(sketch, "E77.bottom", {"start": v(-7239.25, -10) * mm, "end": v(-6539.25, -10) * mm});
            skLineSegment(sketch, "E77.top", {"start": v(-7239.25, 10) * mm, "end": v(-6539.25, 10) * mm});
            skLineSegment(sketch, "E77.left", {"start": v(-7239.25, -10) * mm, "end": v(-7239.25, 10) * mm});
            skLineSegment(sketch, "E77.right", {"start": v(-6539.25, -10) * mm, "end": v(-6539.25, 10) * mm});
            skPoint(sketch, "E77.middle", {"position": v(-6889.25, 0) * mm});
            skSolve(sketch);
        }
        {
            var Q0;
            Q0 = qSketchRegion(id + "F69", true);
            extrude(context, id + "F70", {"entities" : qUnion([Q0]), "depth" : 470 * mm});
        }
        {
            var Q0;
            Q0=makeQuery(id+"F70.opExtrude","SWEPT_FACE",FACE,{"disambiguationData":[OSD([sQuery(id+"F69.wireOp",EDGE,"E77.left")])]});
            var sketch = newSketch(context, id + "F71", { "sketchPlane" : qUnion([Q0])});
            skLineSegment(sketch, "E78.bottom", {"start": v(10, 0) * mm, "end": v(0, 0) * mm});
            skLineSegment(sketch, "E78.top", {"start": v(10, 20) * mm, "end": v(0, 20) * mm});
            skLineSegment(sketch, "E78.left", {"start": v(10, 0) * mm, "end": v(10, 20) * mm});
            skLineSegment(sketch, "E78.right", {"start": v(0, 0) * mm, "end": v(0, 20) * mm});
            skSolve(sketch);
        }
        {
            var Q0;
            Q0 = qSketchRegion(id + "F71", true);
            extrude(context, id + "F72", {"entities" : qUnion([Q0]), "operationType" : NewBodyOperationType.REMOVE, "oppositeDirection" : true, "depth" : 700 * mm});
        }
        {
            var Q0;
            Q0=makeQuery(id+"F70.opExtrude","CAP_FACE",FACE,{"disambiguationData":[OSD([sQuery(id+"F69.wireOp",EDGE,"E77.bottom"),sQuery(id+"F69.wireOp",EDGE,"E77.top"),sQuery(id+"F69.wireOp",EDGE,"E77.left"),sQuery(id+"F69.wireOp",EDGE,"E77.right")])],"isStart":false});
            var sketch = newSketch(context, id + "F73", { "sketchPlane" : qUnion([Q0])});
            skLineSegment(sketch, "E79", {"start": v(-7239.25, 10) * mm, "end": v(-7239.25, -10) * mm});
            skLineSegment(sketch, "E80", {"start": v(-7239.25, -10) * mm, "end": v(-7219.25, -10) * mm});
            skLineSegment(sketch, "E81", {"start": v(-7219.25, -10) * mm, "end": v(-7239.25, 10) * mm});
            skLineSegment(sketch, "E82", {"start": v(-6539.25, 10) * mm, "end": v(-6539.25, -10) * mm});
            skLineSegment(sketch, "E83", {"start": v(-6539.25, -10) * mm, "end": v(-6559.25, -10) * mm});
            skLineSegment(sketch, "E84", {"start": v(-6559.25, -10) * mm, "end": v(-6539.25, 10) * mm});
            skSolve(sketch);
        }
        {
            var Q0;
            Q0 = qSketchRegion(id + "F73", true);
            extrude(context, id + "F74", {"entities" : qUnion([Q0]), "operationType" : NewBodyOperationType.REMOVE, "oppositeDirection" : true, "depth" : 470 * mm});
        }
        {
            var Q0;
            Q0=qCreatedBy(makeId("Top.planeOp"),FACE);
            var sketch = newSketch(context, id + "F75", { "sketchPlane" : qUnion([Q0])});
            skLineSegment(sketch, "E85.bottom", {"start": v(-7458.07, 225) * mm, "end": v(-7438.07, 225) * mm});
            skLineSegment(sketch, "E85.top", {"start": v(-7458.07, -225) * mm, "end": v(-7438.07, -225) * mm});
            skLineSegment(sketch, "E85.left", {"start": v(-7458.07, 225) * mm, "end": v(-7458.07, -225) * mm});
            skLineSegment(sketch, "E85.right", {"start": v(-7438.07, 225) * mm, "end": v(-7438.07, -225) * mm});
            skPoint(sketch, "E85.middle", {"position": v(-7448.07, 0) * mm});
            skSolve(sketch);
        }
        {
            var Q0;
            Q0 = qSketchRegion(id + "F75", true);
            extrude(context, id + "F76", {"entities" : qUnion([Q0]), "depth" : 470 * mm});
        }
        {
            var Q0;
            Q0=makeQuery(id+"F76.opExtrude","CAP_FACE",FACE,{"disambiguationData":[OSD([sQuery(id+"F75.wireOp",EDGE,"E85.bottom"),sQuery(id+"F75.wireOp",EDGE,"E85.top"),sQuery(id+"F75.wireOp",EDGE,"E85.left"),sQuery(id+"F75.wireOp",EDGE,"E85.right")])],"isStart":false});
            var sketch = newSketch(context, id + "F77", { "sketchPlane" : qUnion([Q0])});
            skLineSegment(sketch, "E86", {"start": v(-7438.07, 225) * mm, "end": v(-7458.07, 225) * mm});
            skLineSegment(sketch, "E87", {"start": v(-7458.07, 225) * mm, "end": v(-7458.07, 205) * mm});
            skLineSegment(sketch, "E88", {"start": v(-7458.07, 205) * mm, "end": v(-7438.07, 225) * mm});
            skSolve(sketch);
        }
        {
            var Q0;
            Q0 = qSketchRegion(id + "F77", true);
            extrude(context, id + "F78", {"entities" : qUnion([Q0]), "operationType" : NewBodyOperationType.REMOVE, "oppositeDirection" : true, "depth" : 470 * mm});
        }
        {
            var Q0;
            Q0=makeQuery(id+"F76.opExtrude","SWEPT_FACE",FACE,{"disambiguationData":[OSD([sQuery(id+"F75.wireOp",EDGE,"E85.top")])]});
            var sketch = newSketch(context, id + "F79", { "sketchPlane" : qUnion([Q0])});
            skLineSegment(sketch, "E89.bottom", {"start": v(-7458.07, 0) * mm, "end": v(-7448.07, 0) * mm});
            skLineSegment(sketch, "E89.top", {"start": v(-7458.07, 20) * mm, "end": v(-7448.07, 20) * mm});
            skLineSegment(sketch, "E89.left", {"start": v(-7458.07, 0) * mm, "end": v(-7458.07, 20) * mm});
            skLineSegment(sketch, "E89.right", {"start": v(-7448.07, 0) * mm, "end": v(-7448.07, 20) * mm});
            skSolve(sketch);
        }
        {
            var Q0;
            Q0 = qSketchRegion(id + "F79", true);
            extrude(context, id + "F80", {"entities" : qUnion([Q0]), "operationType" : NewBodyOperationType.REMOVE, "oppositeDirection" : true, "depth" : 450 * mm});
        }
        {
            var Q0;
            Q0=makeQuery(id+"F76.opExtrude","CAP_FACE",FACE,{"disambiguationData":[OSD([sQuery(id+"F75.wireOp",EDGE,"E85.bottom"),sQuery(id+"F75.wireOp",EDGE,"E85.top"),sQuery(id+"F75.wireOp",EDGE,"E85.left"),sQuery(id+"F75.wireOp",EDGE,"E85.right")])],"isStart":false});
            var sketch = newSketch(context, id + "F81", { "sketchPlane" : qUnion([Q0])});
            skLineSegment(sketch, "E90", {"start": v(-7438.07, -225) * mm, "end": v(-7458.07, -225) * mm});
            skLineSegment(sketch, "E91", {"start": v(-7458.07, -225) * mm, "end": v(-7458.07, -205) * mm});
            skLineSegment(sketch, "E92", {"start": v(-7458.07, -205) * mm, "end": v(-7438.07, -225) * mm});
            skSolve(sketch);
        }
        {
            var Q0;
            Q0 = qSketchRegion(id + "F81", true);
            extrude(context, id + "F82", {"entities" : qUnion([Q0]), "operationType" : NewBodyOperationType.REMOVE, "oppositeDirection" : true, "depth" : 170 * mm});
        }
        {
            var Q0;
            Q0=qCreatedBy(makeId("Top.planeOp"),FACE);
            var sketch = newSketch(context, id + "F83", { "sketchPlane" : qUnion([Q0])});
            skLineSegment(sketch, "E93.bottom", {"start": v(-8543.37, -10) * mm, "end": v(-7843.37, -10) * mm});
            skLineSegment(sketch, "E93.top", {"start": v(-8543.37, 10) * mm, "end": v(-7843.37, 10) * mm});
            skLineSegment(sketch, "E93.left", {"start": v(-8543.37, -10) * mm, "end": v(-8543.37, 10) * mm});
            skLineSegment(sketch, "E93.right", {"start": v(-7843.37, -10) * mm, "end": v(-7843.37, 10) * mm});
            skPoint(sketch, "E93.middle", {"position": v(-8193.37, 0) * mm});
            skSolve(sketch);
        }
        {
            var Q0;
            Q0 = qSketchRegion(id + "F83", true);
            extrude(context, id + "F84", {"entities" : qUnion([Q0]), "depth" : 170 * mm});
        }
        {
            var Q0;
            Q0=makeQuery(id+"F84.opExtrude","CAP_FACE",FACE,{"disambiguationData":[OSD([sQuery(id+"F83.wireOp",EDGE,"E93.bottom"),sQuery(id+"F83.wireOp",EDGE,"E93.top"),sQuery(id+"F83.wireOp",EDGE,"E93.left"),sQuery(id+"F83.wireOp",EDGE,"E93.right")])],"isStart":false});
            var sketch = newSketch(context, id + "F85", { "sketchPlane" : qUnion([Q0])});
            skLineSegment(sketch, "E94", {"start": v(-8543.37, -10) * mm, "end": v(-8543.37, 10) * mm});
            skLineSegment(sketch, "E95", {"start": v(-8543.37, 10) * mm, "end": v(-8523.37, 10) * mm});
            skLineSegment(sketch, "E96", {"start": v(-8523.37, 10) * mm, "end": v(-8543.37, -10) * mm});
            skLineSegment(sketch, "E97", {"start": v(-7843.37, -10) * mm, "end": v(-7843.37, 10) * mm});
            skLineSegment(sketch, "E98", {"start": v(-7843.37, 10) * mm, "end": v(-7863.37, 10) * mm});
            skLineSegment(sketch, "E99", {"start": v(-7863.37, 10) * mm, "end": v(-7843.37, -10) * mm});
            skSolve(sketch);
        }
        {
            var Q0;
            Q0 = qSketchRegion(id + "F85", true);
            extrude(context, id + "F86", {"entities" : qUnion([Q0]), "operationType" : NewBodyOperationType.REMOVE, "oppositeDirection" : true, "depth" : 170 * mm});
        }
        {
            var Q0;
            Q0=qCreatedBy(makeId("Top.planeOp"),FACE);
            var sketch = newSketch(context, id + "F87", { "sketchPlane" : qUnion([Q0])});
            skLineSegment(sketch, "E100.bottom", {"start": v(-8999.85, -5) * mm, "end": v(-9659.85, -5) * mm});
            skLineSegment(sketch, "E100.top", {"start": v(-8999.85, 5) * mm, "end": v(-9659.85, 5) * mm});
            skLineSegment(sketch, "E100.left", {"start": v(-8999.85, -5) * mm, "end": v(-8999.85, 5) * mm});
            skLineSegment(sketch, "E100.right", {"start": v(-9659.85, -5) * mm, "end": v(-9659.85, 5) * mm});
            skPoint(sketch, "E100.middle", {"position": v(-9329.85, 0) * mm});
            skSolve(sketch);
        }
        {
            var Q0;
            Q0 = qSketchRegion(id + "F87", true);
            extrude(context, id + "F88", {"entities" : qUnion([Q0]), "depth" : 300 * mm});
        }
        {
            var Q0;
            Q0=qCreatedBy(makeId("Top.planeOp"),FACE);
            var sketch = newSketch(context, id + "F89", { "sketchPlane" : qUnion([Q0])});
            skLineSegment(sketch, "E101.bottom", {"start": v(-10744.88, -65) * mm, "end": v(-10084.88, -65) * mm});
            skLineSegment(sketch, "E101.top", {"start": v(-10744.88, 65) * mm, "end": v(-10084.88, 65) * mm});
            skLineSegment(sketch, "E101.left", {"start": v(-10744.88, -65) * mm, "end": v(-10744.88, 65) * mm});
            skLineSegment(sketch, "E101.right", {"start": v(-10084.88, -65) * mm, "end": v(-10084.88, 65) * mm});
            skPoint(sketch, "E101.middle", {"position": v(-10414.88, 0) * mm});
            skSolve(sketch);
        }
        {
            var Q0;
            Q0 = qSketchRegion(id + "F89", true);
            extrude(context, id + "F90", {"entities" : qUnion([Q0]), "depth" : 20 * mm});
        }
        {
            var Q0;
            Q0=qCreatedBy(makeId("Top.planeOp"),FACE);
            var sketch = newSketch(context, id + "F91", { "sketchPlane" : qUnion([Q0])});
            skLineSegment(sketch, "E102.bottom", {"start": v(-11751.37, -5) * mm, "end": v(-11091.37, -5) * mm});
            skLineSegment(sketch, "E102.top", {"start": v(-11751.37, 5) * mm, "end": v(-11091.37, 5) * mm});
            skLineSegment(sketch, "E102.left", {"start": v(-11751.37, -5) * mm, "end": v(-11751.37, 5) * mm});
            skLineSegment(sketch, "E102.right", {"start": v(-11091.37, -5) * mm, "end": v(-11091.37, 5) * mm});
            skPoint(sketch, "E102.middle", {"position": v(-11421.37, 0) * mm});
            skSolve(sketch);
        }
        {
            var Q0;
            Q0 = qSketchRegion(id + "F91", true);
            extrude(context, id + "F92", {"entities" : qUnion([Q0]), "depth" : 320 * mm});
        }
        {
            var Q0;
            Q0=qCreatedBy(makeId("Top.planeOp"),FACE);
            var sketch = newSketch(context, id + "F93", { "sketchPlane" : qUnion([Q0])});
            skLineSegment(sketch, "E103.bottom", {"start": v(-12755.71, -62.5) * mm, "end": v(-12095.71, -62.5) * mm});
            skLineSegment(sketch, "E103.top", {"start": v(-12755.71, 62.5) * mm, "end": v(-12095.71, 62.5) * mm});
            skLineSegment(sketch, "E103.left", {"start": v(-12755.71, -62.5) * mm, "end": v(-12755.71, 62.5) * mm});
            skLineSegment(sketch, "E103.right", {"start": v(-12095.71, -62.5) * mm, "end": v(-12095.71, 62.5) * mm});
            skPoint(sketch, "E103.middle", {"position": v(-12425.71, 0) * mm});
            skSolve(sketch);
        }
        {
            var Q0;
            Q0 = qSketchRegion(id + "F93", true);
            extrude(context, id + "F94", {"entities" : qUnion([Q0]), "depth" : 142 * mm});
        }
        {
            var Q0;
            Q0=makeQuery(id+"F94.opExtrude","CAP_FACE",FACE,{"disambiguationData":[OSD([sQuery(id+"F93.wireOp",EDGE,"E103.bottom"),sQuery(id+"F93.wireOp",EDGE,"E103.top"),sQuery(id+"F93.wireOp",EDGE,"E103.left"),sQuery(id+"F93.wireOp",EDGE,"E103.right")])],"isStart":false});
            var sketch = newSketch(context, id + "F95", { "sketchPlane" : qUnion([Q0])});
            skLineSegment(sketch, "E104.bottom", {"start": v(-12746.21, 62.5) * mm, "end": v(-12745.71, 62.5) * mm});
            skLineSegment(sketch, "E104.top", {"start": v(-12746.21, -62.5) * mm, "end": v(-12745.71, -62.5) * mm});
            skLineSegment(sketch, "E104.left", {"start": v(-12746.21, 62.5) * mm, "end": v(-12746.21, -62.5) * mm});
            skLineSegment(sketch, "E104.right", {"start": v(-12745.71, 62.5) * mm, "end": v(-12745.71, -62.5) * mm});
            skLineSegment(sketch, "E105.1.0.0", {"start": v(-12736.21, 62.5) * mm, "end": v(-12736.21, -62.5) * mm});
            skLineSegment(sketch, "E105.1.0.1", {"start": v(-12735.71, 62.5) * mm, "end": v(-12735.71, -62.5) * mm});
            skLineSegment(sketch, "E105.1.0.2", {"start": v(-12736.21, 62.5) * mm, "end": v(-12735.71, 62.5) * mm});
            skLineSegment(sketch, "E105.1.0.3", {"start": v(-12736.21, -62.5) * mm, "end": v(-12735.71, -62.5) * mm});
            skLineSegment(sketch, "E105.2.0.0", {"start": v(-12726.21, 62.5) * mm, "end": v(-12726.21, -62.5) * mm});
            skLineSegment(sketch, "E105.2.0.1", {"start": v(-12725.71, 62.5) * mm, "end": v(-12725.71, -62.5) * mm});
            skLineSegment(sketch, "E105.2.0.2", {"start": v(-12726.21, 62.5) * mm, "end": v(-12725.71, 62.5) * mm});
            skLineSegment(sketch, "E105.2.0.3", {"start": v(-12726.21, -62.5) * mm, "end": v(-12725.71, -62.5) * mm});
            skLineSegment(sketch, "E105.3.0.0", {"start": v(-12716.21, 62.5) * mm, "end": v(-12716.21, -62.5) * mm});
            skLineSegment(sketch, "E105.3.0.1", {"start": v(-12715.71, 62.5) * mm, "end": v(-12715.71, -62.5) * mm});
            skLineSegment(sketch, "E105.3.0.2", {"start": v(-12716.21, 62.5) * mm, "end": v(-12715.71, 62.5) * mm});
            skLineSegment(sketch, "E105.3.0.3", {"start": v(-12716.21, -62.5) * mm, "end": v(-12715.71, -62.5) * mm});
            skLineSegment(sketch, "E105.4.0.0", {"start": v(-12706.21, 62.5) * mm, "end": v(-12706.21, -62.5) * mm});
            skLineSegment(sketch, "E105.4.0.1", {"start": v(-12705.71, 62.5) * mm, "end": v(-12705.71, -62.5) * mm});
            skLineSegment(sketch, "E105.4.0.2", {"start": v(-12706.21, 62.5) * mm, "end": v(-12705.71, 62.5) * mm});
            skLineSegment(sketch, "E105.4.0.3", {"start": v(-12706.21, -62.5) * mm, "end": v(-12705.71, -62.5) * mm});
            skLineSegment(sketch, "E105.5.0.0", {"start": v(-12696.21, 62.5) * mm, "end": v(-12696.21, -62.5) * mm});
            skLineSegment(sketch, "E105.5.0.1", {"start": v(-12695.71, 62.5) * mm, "end": v(-12695.71, -62.5) * mm});
            skLineSegment(sketch, "E105.5.0.2", {"start": v(-12696.21, 62.5) * mm, "end": v(-12695.71, 62.5) * mm});
            skLineSegment(sketch, "E105.5.0.3", {"start": v(-12696.21, -62.5) * mm, "end": v(-12695.71, -62.5) * mm});
            skLineSegment(sketch, "E105.6.0.0", {"start": v(-12686.21, 62.5) * mm, "end": v(-12686.21, -62.5) * mm});
            skLineSegment(sketch, "E105.6.0.1", {"start": v(-12685.71, 62.5) * mm, "end": v(-12685.71, -62.5) * mm});
            skLineSegment(sketch, "E105.6.0.2", {"start": v(-12686.21, 62.5) * mm, "end": v(-12685.71, 62.5) * mm});
            skLineSegment(sketch, "E105.6.0.3", {"start": v(-12686.21, -62.5) * mm, "end": v(-12685.71, -62.5) * mm});
            skLineSegment(sketch, "E105.7.0.0", {"start": v(-12676.21, 62.5) * mm, "end": v(-12676.21, -62.5) * mm});
            skLineSegment(sketch, "E105.7.0.1", {"start": v(-12675.71, 62.5) * mm, "end": v(-12675.71, -62.5) * mm});
            skLineSegment(sketch, "E105.7.0.2", {"start": v(-12676.21, 62.5) * mm, "end": v(-12675.71, 62.5) * mm});
            skLineSegment(sketch, "E105.7.0.3", {"start": v(-12676.21, -62.5) * mm, "end": v(-12675.71, -62.5) * mm});
            skLineSegment(sketch, "E105.8.0.0", {"start": v(-12666.21, 62.5) * mm, "end": v(-12666.21, -62.5) * mm});
            skLineSegment(sketch, "E105.8.0.1", {"start": v(-12665.71, 62.5) * mm, "end": v(-12665.71, -62.5) * mm});
            skLineSegment(sketch, "E105.8.0.2", {"start": v(-12666.21, 62.5) * mm, "end": v(-12665.71, 62.5) * mm});
            skLineSegment(sketch, "E105.8.0.3", {"start": v(-12666.21, -62.5) * mm, "end": v(-12665.71, -62.5) * mm});
            skLineSegment(sketch, "E105.9.0.0", {"start": v(-12656.21, 62.5) * mm, "end": v(-12656.21, -62.5) * mm});
            skLineSegment(sketch, "E105.9.0.1", {"start": v(-12655.71, 62.5) * mm, "end": v(-12655.71, -62.5) * mm});
            skLineSegment(sketch, "E105.9.0.2", {"start": v(-12656.21, 62.5) * mm, "end": v(-12655.71, 62.5) * mm});
            skLineSegment(sketch, "E105.9.0.3", {"start": v(-12656.21, -62.5) * mm, "end": v(-12655.71, -62.5) * mm});
            skLineSegment(sketch, "E105.10.0.0", {"start": v(-12646.21, 62.5) * mm, "end": v(-12646.21, -62.5) * mm});
            skLineSegment(sketch, "E105.10.0.1", {"start": v(-12645.71, 62.5) * mm, "end": v(-12645.71, -62.5) * mm});
            skLineSegment(sketch, "E105.10.0.2", {"start": v(-12646.21, 62.5) * mm, "end": v(-12645.71, 62.5) * mm});
            skLineSegment(sketch, "E105.10.0.3", {"start": v(-12646.21, -62.5) * mm, "end": v(-12645.71, -62.5) * mm});
            skLineSegment(sketch, "E105.11.0.0", {"start": v(-12636.21, 62.5) * mm, "end": v(-12636.21, -62.5) * mm});
            skLineSegment(sketch, "E105.11.0.1", {"start": v(-12635.71, 62.5) * mm, "end": v(-12635.71, -62.5) * mm});
            skLineSegment(sketch, "E105.11.0.2", {"start": v(-12636.21, 62.5) * mm, "end": v(-12635.71, 62.5) * mm});
            skLineSegment(sketch, "E105.11.0.3", {"start": v(-12636.21, -62.5) * mm, "end": v(-12635.71, -62.5) * mm});
            skLineSegment(sketch, "E105.12.0.0", {"start": v(-12626.21, 62.5) * mm, "end": v(-12626.21, -62.5) * mm});
            skLineSegment(sketch, "E105.12.0.1", {"start": v(-12625.71, 62.5) * mm, "end": v(-12625.71, -62.5) * mm});
            skLineSegment(sketch, "E105.12.0.2", {"start": v(-12626.21, 62.5) * mm, "end": v(-12625.71, 62.5) * mm});
            skLineSegment(sketch, "E105.12.0.3", {"start": v(-12626.21, -62.5) * mm, "end": v(-12625.71, -62.5) * mm});
            skLineSegment(sketch, "E105.13.0.0", {"start": v(-12616.21, 62.5) * mm, "end": v(-12616.21, -62.5) * mm});
            skLineSegment(sketch, "E105.13.0.1", {"start": v(-12615.71, 62.5) * mm, "end": v(-12615.71, -62.5) * mm});
            skLineSegment(sketch, "E105.13.0.2", {"start": v(-12616.21, 62.5) * mm, "end": v(-12615.71, 62.5) * mm});
            skLineSegment(sketch, "E105.13.0.3", {"start": v(-12616.21, -62.5) * mm, "end": v(-12615.71, -62.5) * mm});
            skLineSegment(sketch, "E105.14.0.0", {"start": v(-12606.21, 62.5) * mm, "end": v(-12606.21, -62.5) * mm});
            skLineSegment(sketch, "E105.14.0.1", {"start": v(-12605.71, 62.5) * mm, "end": v(-12605.71, -62.5) * mm});
            skLineSegment(sketch, "E105.14.0.2", {"start": v(-12606.21, 62.5) * mm, "end": v(-12605.71, 62.5) * mm});
            skLineSegment(sketch, "E105.14.0.3", {"start": v(-12606.21, -62.5) * mm, "end": v(-12605.71, -62.5) * mm});
            skLineSegment(sketch, "E105.15.0.0", {"start": v(-12596.21, 62.5) * mm, "end": v(-12596.21, -62.5) * mm});
            skLineSegment(sketch, "E105.15.0.1", {"start": v(-12595.71, 62.5) * mm, "end": v(-12595.71, -62.5) * mm});
            skLineSegment(sketch, "E105.15.0.2", {"start": v(-12596.21, 62.5) * mm, "end": v(-12595.71, 62.5) * mm});
            skLineSegment(sketch, "E105.15.0.3", {"start": v(-12596.21, -62.5) * mm, "end": v(-12595.71, -62.5) * mm});
            skLineSegment(sketch, "E105.16.0.0", {"start": v(-12586.21, 62.5) * mm, "end": v(-12586.21, -62.5) * mm});
            skLineSegment(sketch, "E105.16.0.1", {"start": v(-12585.71, 62.5) * mm, "end": v(-12585.71, -62.5) * mm});
            skLineSegment(sketch, "E105.16.0.2", {"start": v(-12586.21, 62.5) * mm, "end": v(-12585.71, 62.5) * mm});
            skLineSegment(sketch, "E105.16.0.3", {"start": v(-12586.21, -62.5) * mm, "end": v(-12585.71, -62.5) * mm});
            skLineSegment(sketch, "E105.17.0.0", {"start": v(-12576.21, 62.5) * mm, "end": v(-12576.21, -62.5) * mm});
            skLineSegment(sketch, "E105.17.0.1", {"start": v(-12575.71, 62.5) * mm, "end": v(-12575.71, -62.5) * mm});
            skLineSegment(sketch, "E105.17.0.2", {"start": v(-12576.21, 62.5) * mm, "end": v(-12575.71, 62.5) * mm});
            skLineSegment(sketch, "E105.17.0.3", {"start": v(-12576.21, -62.5) * mm, "end": v(-12575.71, -62.5) * mm});
            skLineSegment(sketch, "E105.18.0.0", {"start": v(-12566.21, 62.5) * mm, "end": v(-12566.21, -62.5) * mm});
            skLineSegment(sketch, "E105.18.0.1", {"start": v(-12565.71, 62.5) * mm, "end": v(-12565.71, -62.5) * mm});
            skLineSegment(sketch, "E105.18.0.2", {"start": v(-12566.21, 62.5) * mm, "end": v(-12565.71, 62.5) * mm});
            skLineSegment(sketch, "E105.18.0.3", {"start": v(-12566.21, -62.5) * mm, "end": v(-12565.71, -62.5) * mm});
            skLineSegment(sketch, "E105.19.0.0", {"start": v(-12556.21, 62.5) * mm, "end": v(-12556.21, -62.5) * mm});
            skLineSegment(sketch, "E105.19.0.1", {"start": v(-12555.71, 62.5) * mm, "end": v(-12555.71, -62.5) * mm});
            skLineSegment(sketch, "E105.19.0.2", {"start": v(-12556.21, 62.5) * mm, "end": v(-12555.71, 62.5) * mm});
            skLineSegment(sketch, "E105.19.0.3", {"start": v(-12556.21, -62.5) * mm, "end": v(-12555.71, -62.5) * mm});
            skLineSegment(sketch, "E105.20.0.0", {"start": v(-12546.21, 62.5) * mm, "end": v(-12546.21, -62.5) * mm});
            skLineSegment(sketch, "E105.20.0.1", {"start": v(-12545.71, 62.5) * mm, "end": v(-12545.71, -62.5) * mm});
            skLineSegment(sketch, "E105.20.0.2", {"start": v(-12546.21, 62.5) * mm, "end": v(-12545.71, 62.5) * mm});
            skLineSegment(sketch, "E105.20.0.3", {"start": v(-12546.21, -62.5) * mm, "end": v(-12545.71, -62.5) * mm});
            skLineSegment(sketch, "E105.21.0.0", {"start": v(-12536.21, 62.5) * mm, "end": v(-12536.21, -62.5) * mm});
            skLineSegment(sketch, "E105.21.0.1", {"start": v(-12535.71, 62.5) * mm, "end": v(-12535.71, -62.5) * mm});
            skLineSegment(sketch, "E105.21.0.2", {"start": v(-12536.21, 62.5) * mm, "end": v(-12535.71, 62.5) * mm});
            skLineSegment(sketch, "E105.21.0.3", {"start": v(-12536.21, -62.5) * mm, "end": v(-12535.71, -62.5) * mm});
            skLineSegment(sketch, "E105.22.0.0", {"start": v(-12526.21, 62.5) * mm, "end": v(-12526.21, -62.5) * mm});
            skLineSegment(sketch, "E105.22.0.1", {"start": v(-12525.71, 62.5) * mm, "end": v(-12525.71, -62.5) * mm});
            skLineSegment(sketch, "E105.22.0.2", {"start": v(-12526.21, 62.5) * mm, "end": v(-12525.71, 62.5) * mm});
            skLineSegment(sketch, "E105.22.0.3", {"start": v(-12526.21, -62.5) * mm, "end": v(-12525.71, -62.5) * mm});
            skLineSegment(sketch, "E105.23.0.0", {"start": v(-12516.21, 62.5) * mm, "end": v(-12516.21, -62.5) * mm});
            skLineSegment(sketch, "E105.23.0.1", {"start": v(-12515.71, 62.5) * mm, "end": v(-12515.71, -62.5) * mm});
            skLineSegment(sketch, "E105.23.0.2", {"start": v(-12516.21, 62.5) * mm, "end": v(-12515.71, 62.5) * mm});
            skLineSegment(sketch, "E105.23.0.3", {"start": v(-12516.21, -62.5) * mm, "end": v(-12515.71, -62.5) * mm});
            skLineSegment(sketch, "E105.24.0.0", {"start": v(-12506.21, 62.5) * mm, "end": v(-12506.21, -62.5) * mm});
            skLineSegment(sketch, "E105.24.0.1", {"start": v(-12505.71, 62.5) * mm, "end": v(-12505.71, -62.5) * mm});
            skLineSegment(sketch, "E105.24.0.2", {"start": v(-12506.21, 62.5) * mm, "end": v(-12505.71, 62.5) * mm});
            skLineSegment(sketch, "E105.24.0.3", {"start": v(-12506.21, -62.5) * mm, "end": v(-12505.71, -62.5) * mm});
            skLineSegment(sketch, "E105.25.0.0", {"start": v(-12496.21, 62.5) * mm, "end": v(-12496.21, -62.5) * mm});
            skLineSegment(sketch, "E105.25.0.1", {"start": v(-12495.71, 62.5) * mm, "end": v(-12495.71, -62.5) * mm});
            skLineSegment(sketch, "E105.25.0.2", {"start": v(-12496.21, 62.5) * mm, "end": v(-12495.71, 62.5) * mm});
            skLineSegment(sketch, "E105.25.0.3", {"start": v(-12496.21, -62.5) * mm, "end": v(-12495.71, -62.5) * mm});
            skLineSegment(sketch, "E105.26.0.0", {"start": v(-12486.21, 62.5) * mm, "end": v(-12486.21, -62.5) * mm});
            skLineSegment(sketch, "E105.26.0.1", {"start": v(-12485.71, 62.5) * mm, "end": v(-12485.71, -62.5) * mm});
            skLineSegment(sketch, "E105.26.0.2", {"start": v(-12486.21, 62.5) * mm, "end": v(-12485.71, 62.5) * mm});
            skLineSegment(sketch, "E105.26.0.3", {"start": v(-12486.21, -62.5) * mm, "end": v(-12485.71, -62.5) * mm});
            skLineSegment(sketch, "E105.27.0.0", {"start": v(-12476.21, 62.5) * mm, "end": v(-12476.21, -62.5) * mm});
            skLineSegment(sketch, "E105.27.0.1", {"start": v(-12475.71, 62.5) * mm, "end": v(-12475.71, -62.5) * mm});
            skLineSegment(sketch, "E105.27.0.2", {"start": v(-12476.21, 62.5) * mm, "end": v(-12475.71, 62.5) * mm});
            skLineSegment(sketch, "E105.27.0.3", {"start": v(-12476.21, -62.5) * mm, "end": v(-12475.71, -62.5) * mm});
            skLineSegment(sketch, "E105.28.0.0", {"start": v(-12466.21, 62.5) * mm, "end": v(-12466.21, -62.5) * mm});
            skLineSegment(sketch, "E105.28.0.1", {"start": v(-12465.71, 62.5) * mm, "end": v(-12465.71, -62.5) * mm});
            skLineSegment(sketch, "E105.28.0.2", {"start": v(-12466.21, 62.5) * mm, "end": v(-12465.71, 62.5) * mm});
            skLineSegment(sketch, "E105.28.0.3", {"start": v(-12466.21, -62.5) * mm, "end": v(-12465.71, -62.5) * mm});
            skLineSegment(sketch, "E105.29.0.0", {"start": v(-12456.21, 62.5) * mm, "end": v(-12456.21, -62.5) * mm});
            skLineSegment(sketch, "E105.29.0.1", {"start": v(-12455.71, 62.5) * mm, "end": v(-12455.71, -62.5) * mm});
            skLineSegment(sketch, "E105.29.0.2", {"start": v(-12456.21, 62.5) * mm, "end": v(-12455.71, 62.5) * mm});
            skLineSegment(sketch, "E105.29.0.3", {"start": v(-12456.21, -62.5) * mm, "end": v(-12455.71, -62.5) * mm});
            skLineSegment(sketch, "E105.30.0.0", {"start": v(-12446.21, 62.5) * mm, "end": v(-12446.21, -62.5) * mm});
            skLineSegment(sketch, "E105.30.0.1", {"start": v(-12445.71, 62.5) * mm, "end": v(-12445.71, -62.5) * mm});
            skLineSegment(sketch, "E105.30.0.2", {"start": v(-12446.21, 62.5) * mm, "end": v(-12445.71, 62.5) * mm});
            skLineSegment(sketch, "E105.30.0.3", {"start": v(-12446.21, -62.5) * mm, "end": v(-12445.71, -62.5) * mm});
            skLineSegment(sketch, "E105.31.0.0", {"start": v(-12436.21, 62.5) * mm, "end": v(-12436.21, -62.5) * mm});
            skLineSegment(sketch, "E105.31.0.1", {"start": v(-12435.71, 62.5) * mm, "end": v(-12435.71, -62.5) * mm});
            skLineSegment(sketch, "E105.31.0.2", {"start": v(-12436.21, 62.5) * mm, "end": v(-12435.71, 62.5) * mm});
            skLineSegment(sketch, "E105.31.0.3", {"start": v(-12436.21, -62.5) * mm, "end": v(-12435.71, -62.5) * mm});
            skLineSegment(sketch, "E105.32.0.0", {"start": v(-12426.21, 62.5) * mm, "end": v(-12426.21, -62.5) * mm});
            skLineSegment(sketch, "E105.32.0.1", {"start": v(-12425.71, 62.5) * mm, "end": v(-12425.71, -62.5) * mm});
            skLineSegment(sketch, "E105.32.0.2", {"start": v(-12426.21, 62.5) * mm, "end": v(-12425.71, 62.5) * mm});
            skLineSegment(sketch, "E105.32.0.3", {"start": v(-12426.21, -62.5) * mm, "end": v(-12425.71, -62.5) * mm});
            skLineSegment(sketch, "E105.33.0.0", {"start": v(-12416.21, 62.5) * mm, "end": v(-12416.21, -62.5) * mm});
            skLineSegment(sketch, "E105.33.0.1", {"start": v(-12415.71, 62.5) * mm, "end": v(-12415.71, -62.5) * mm});
            skLineSegment(sketch, "E105.33.0.2", {"start": v(-12416.21, 62.5) * mm, "end": v(-12415.71, 62.5) * mm});
            skLineSegment(sketch, "E105.33.0.3", {"start": v(-12416.21, -62.5) * mm, "end": v(-12415.71, -62.5) * mm});
            skLineSegment(sketch, "E105.34.0.0", {"start": v(-12406.21, 62.5) * mm, "end": v(-12406.21, -62.5) * mm});
            skLineSegment(sketch, "E105.34.0.1", {"start": v(-12405.71, 62.5) * mm, "end": v(-12405.71, -62.5) * mm});
            skLineSegment(sketch, "E105.34.0.2", {"start": v(-12406.21, 62.5) * mm, "end": v(-12405.71, 62.5) * mm});
            skLineSegment(sketch, "E105.34.0.3", {"start": v(-12406.21, -62.5) * mm, "end": v(-12405.71, -62.5) * mm});
            skLineSegment(sketch, "E105.35.0.0", {"start": v(-12396.21, 62.5) * mm, "end": v(-12396.21, -62.5) * mm});
            skLineSegment(sketch, "E105.35.0.1", {"start": v(-12395.71, 62.5) * mm, "end": v(-12395.71, -62.5) * mm});
            skLineSegment(sketch, "E105.35.0.2", {"start": v(-12396.21, 62.5) * mm, "end": v(-12395.71, 62.5) * mm});
            skLineSegment(sketch, "E105.35.0.3", {"start": v(-12396.21, -62.5) * mm, "end": v(-12395.71, -62.5) * mm});
            skLineSegment(sketch, "E105.36.0.0", {"start": v(-12386.21, 62.5) * mm, "end": v(-12386.21, -62.5) * mm});
            skLineSegment(sketch, "E105.36.0.1", {"start": v(-12385.71, 62.5) * mm, "end": v(-12385.71, -62.5) * mm});
            skLineSegment(sketch, "E105.36.0.2", {"start": v(-12386.21, 62.5) * mm, "end": v(-12385.71, 62.5) * mm});
            skLineSegment(sketch, "E105.36.0.3", {"start": v(-12386.21, -62.5) * mm, "end": v(-12385.71, -62.5) * mm});
            skLineSegment(sketch, "E105.37.0.0", {"start": v(-12376.21, 62.5) * mm, "end": v(-12376.21, -62.5) * mm});
            skLineSegment(sketch, "E105.37.0.1", {"start": v(-12375.71, 62.5) * mm, "end": v(-12375.71, -62.5) * mm});
            skLineSegment(sketch, "E105.37.0.2", {"start": v(-12376.21, 62.5) * mm, "end": v(-12375.71, 62.5) * mm});
            skLineSegment(sketch, "E105.37.0.3", {"start": v(-12376.21, -62.5) * mm, "end": v(-12375.71, -62.5) * mm});
            skLineSegment(sketch, "E105.38.0.0", {"start": v(-12366.21, 62.5) * mm, "end": v(-12366.21, -62.5) * mm});
            skLineSegment(sketch, "E105.38.0.1", {"start": v(-12365.71, 62.5) * mm, "end": v(-12365.71, -62.5) * mm});
            skLineSegment(sketch, "E105.38.0.2", {"start": v(-12366.21, 62.5) * mm, "end": v(-12365.71, 62.5) * mm});
            skLineSegment(sketch, "E105.38.0.3", {"start": v(-12366.21, -62.5) * mm, "end": v(-12365.71, -62.5) * mm});
            skLineSegment(sketch, "E105.39.0.0", {"start": v(-12356.21, 62.5) * mm, "end": v(-12356.21, -62.5) * mm});
            skLineSegment(sketch, "E105.39.0.1", {"start": v(-12355.71, 62.5) * mm, "end": v(-12355.71, -62.5) * mm});
            skLineSegment(sketch, "E105.39.0.2", {"start": v(-12356.21, 62.5) * mm, "end": v(-12355.71, 62.5) * mm});
            skLineSegment(sketch, "E105.39.0.3", {"start": v(-12356.21, -62.5) * mm, "end": v(-12355.71, -62.5) * mm});
            skLineSegment(sketch, "E105.40.0.0", {"start": v(-12346.21, 62.5) * mm, "end": v(-12346.21, -62.5) * mm});
            skLineSegment(sketch, "E105.40.0.1", {"start": v(-12345.71, 62.5) * mm, "end": v(-12345.71, -62.5) * mm});
            skLineSegment(sketch, "E105.40.0.2", {"start": v(-12346.21, 62.5) * mm, "end": v(-12345.71, 62.5) * mm});
            skLineSegment(sketch, "E105.40.0.3", {"start": v(-12346.21, -62.5) * mm, "end": v(-12345.71, -62.5) * mm});
            skLineSegment(sketch, "E105.41.0.0", {"start": v(-12336.21, 62.5) * mm, "end": v(-12336.21, -62.5) * mm});
            skLineSegment(sketch, "E105.41.0.1", {"start": v(-12335.71, 62.5) * mm, "end": v(-12335.71, -62.5) * mm});
            skLineSegment(sketch, "E105.41.0.2", {"start": v(-12336.21, 62.5) * mm, "end": v(-12335.71, 62.5) * mm});
            skLineSegment(sketch, "E105.41.0.3", {"start": v(-12336.21, -62.5) * mm, "end": v(-12335.71, -62.5) * mm});
            skLineSegment(sketch, "E105.42.0.0", {"start": v(-12326.21, 62.5) * mm, "end": v(-12326.21, -62.5) * mm});
            skLineSegment(sketch, "E105.42.0.1", {"start": v(-12325.71, 62.5) * mm, "end": v(-12325.71, -62.5) * mm});
            skLineSegment(sketch, "E105.42.0.2", {"start": v(-12326.21, 62.5) * mm, "end": v(-12325.71, 62.5) * mm});
            skLineSegment(sketch, "E105.42.0.3", {"start": v(-12326.21, -62.5) * mm, "end": v(-12325.71, -62.5) * mm});
            skLineSegment(sketch, "E105.43.0.0", {"start": v(-12316.21, 62.5) * mm, "end": v(-12316.21, -62.5) * mm});
            skLineSegment(sketch, "E105.43.0.1", {"start": v(-12315.71, 62.5) * mm, "end": v(-12315.71, -62.5) * mm});
            skLineSegment(sketch, "E105.43.0.2", {"start": v(-12316.21, 62.5) * mm, "end": v(-12315.71, 62.5) * mm});
            skLineSegment(sketch, "E105.43.0.3", {"start": v(-12316.21, -62.5) * mm, "end": v(-12315.71, -62.5) * mm});
            skLineSegment(sketch, "E105.44.0.0", {"start": v(-12306.21, 62.5) * mm, "end": v(-12306.21, -62.5) * mm});
            skLineSegment(sketch, "E105.44.0.1", {"start": v(-12305.71, 62.5) * mm, "end": v(-12305.71, -62.5) * mm});
            skLineSegment(sketch, "E105.44.0.2", {"start": v(-12306.21, 62.5) * mm, "end": v(-12305.71, 62.5) * mm});
            skLineSegment(sketch, "E105.44.0.3", {"start": v(-12306.21, -62.5) * mm, "end": v(-12305.71, -62.5) * mm});
            skLineSegment(sketch, "E105.45.0.0", {"start": v(-12296.21, 62.5) * mm, "end": v(-12296.21, -62.5) * mm});
            skLineSegment(sketch, "E105.45.0.1", {"start": v(-12295.71, 62.5) * mm, "end": v(-12295.71, -62.5) * mm});
            skLineSegment(sketch, "E105.45.0.2", {"start": v(-12296.21, 62.5) * mm, "end": v(-12295.71, 62.5) * mm});
            skLineSegment(sketch, "E105.45.0.3", {"start": v(-12296.21, -62.5) * mm, "end": v(-12295.71, -62.5) * mm});
            skLineSegment(sketch, "E105.46.0.0", {"start": v(-12286.21, 62.5) * mm, "end": v(-12286.21, -62.5) * mm});
            skLineSegment(sketch, "E105.46.0.1", {"start": v(-12285.71, 62.5) * mm, "end": v(-12285.71, -62.5) * mm});
            skLineSegment(sketch, "E105.46.0.2", {"start": v(-12286.21, 62.5) * mm, "end": v(-12285.71, 62.5) * mm});
            skLineSegment(sketch, "E105.46.0.3", {"start": v(-12286.21, -62.5) * mm, "end": v(-12285.71, -62.5) * mm});
            skLineSegment(sketch, "E105.47.0.0", {"start": v(-12276.21, 62.5) * mm, "end": v(-12276.21, -62.5) * mm});
            skLineSegment(sketch, "E105.47.0.1", {"start": v(-12275.71, 62.5) * mm, "end": v(-12275.71, -62.5) * mm});
            skLineSegment(sketch, "E105.47.0.2", {"start": v(-12276.21, 62.5) * mm, "end": v(-12275.71, 62.5) * mm});
            skLineSegment(sketch, "E105.47.0.3", {"start": v(-12276.21, -62.5) * mm, "end": v(-12275.71, -62.5) * mm});
            skLineSegment(sketch, "E105.48.0.0", {"start": v(-12266.21, 62.5) * mm, "end": v(-12266.21, -62.5) * mm});
            skLineSegment(sketch, "E105.48.0.1", {"start": v(-12265.71, 62.5) * mm, "end": v(-12265.71, -62.5) * mm});
            skLineSegment(sketch, "E105.48.0.2", {"start": v(-12266.21, 62.5) * mm, "end": v(-12265.71, 62.5) * mm});
            skLineSegment(sketch, "E105.48.0.3", {"start": v(-12266.21, -62.5) * mm, "end": v(-12265.71, -62.5) * mm});
            skLineSegment(sketch, "E105.49.0.0", {"start": v(-12256.21, 62.5) * mm, "end": v(-12256.21, -62.5) * mm});
            skLineSegment(sketch, "E105.49.0.1", {"start": v(-12255.71, 62.5) * mm, "end": v(-12255.71, -62.5) * mm});
            skLineSegment(sketch, "E105.49.0.2", {"start": v(-12256.21, 62.5) * mm, "end": v(-12255.71, 62.5) * mm});
            skLineSegment(sketch, "E105.49.0.3", {"start": v(-12256.21, -62.5) * mm, "end": v(-12255.71, -62.5) * mm});
            skLineSegment(sketch, "E105.50.0.0", {"start": v(-12246.21, 62.5) * mm, "end": v(-12246.21, -62.5) * mm});
            skLineSegment(sketch, "E105.50.0.1", {"start": v(-12245.71, 62.5) * mm, "end": v(-12245.71, -62.5) * mm});
            skLineSegment(sketch, "E105.50.0.2", {"start": v(-12246.21, 62.5) * mm, "end": v(-12245.71, 62.5) * mm});
            skLineSegment(sketch, "E105.50.0.3", {"start": v(-12246.21, -62.5) * mm, "end": v(-12245.71, -62.5) * mm});
            skLineSegment(sketch, "E105.51.0.0", {"start": v(-12236.21, 62.5) * mm, "end": v(-12236.21, -62.5) * mm});
            skLineSegment(sketch, "E105.51.0.1", {"start": v(-12235.71, 62.5) * mm, "end": v(-12235.71, -62.5) * mm});
            skLineSegment(sketch, "E105.51.0.2", {"start": v(-12236.21, 62.5) * mm, "end": v(-12235.71, 62.5) * mm});
            skLineSegment(sketch, "E105.51.0.3", {"start": v(-12236.21, -62.5) * mm, "end": v(-12235.71, -62.5) * mm});
            skLineSegment(sketch, "E105.52.0.0", {"start": v(-12226.21, 62.5) * mm, "end": v(-12226.21, -62.5) * mm});
            skLineSegment(sketch, "E105.52.0.1", {"start": v(-12225.71, 62.5) * mm, "end": v(-12225.71, -62.5) * mm});
            skLineSegment(sketch, "E105.52.0.2", {"start": v(-12226.21, 62.5) * mm, "end": v(-12225.71, 62.5) * mm});
            skLineSegment(sketch, "E105.52.0.3", {"start": v(-12226.21, -62.5) * mm, "end": v(-12225.71, -62.5) * mm});
            skLineSegment(sketch, "E105.53.0.0", {"start": v(-12216.21, 62.5) * mm, "end": v(-12216.21, -62.5) * mm});
            skLineSegment(sketch, "E105.53.0.1", {"start": v(-12215.71, 62.5) * mm, "end": v(-12215.71, -62.5) * mm});
            skLineSegment(sketch, "E105.53.0.2", {"start": v(-12216.21, 62.5) * mm, "end": v(-12215.71, 62.5) * mm});
            skLineSegment(sketch, "E105.53.0.3", {"start": v(-12216.21, -62.5) * mm, "end": v(-12215.71, -62.5) * mm});
            skLineSegment(sketch, "E105.54.0.0", {"start": v(-12206.21, 62.5) * mm, "end": v(-12206.21, -62.5) * mm});
            skLineSegment(sketch, "E105.54.0.1", {"start": v(-12205.71, 62.5) * mm, "end": v(-12205.71, -62.5) * mm});
            skLineSegment(sketch, "E105.54.0.2", {"start": v(-12206.21, 62.5) * mm, "end": v(-12205.71, 62.5) * mm});
            skLineSegment(sketch, "E105.54.0.3", {"start": v(-12206.21, -62.5) * mm, "end": v(-12205.71, -62.5) * mm});
            skLineSegment(sketch, "E105.55.0.0", {"start": v(-12196.21, 62.5) * mm, "end": v(-12196.21, -62.5) * mm});
            skLineSegment(sketch, "E105.55.0.1", {"start": v(-12195.71, 62.5) * mm, "end": v(-12195.71, -62.5) * mm});
            skLineSegment(sketch, "E105.55.0.2", {"start": v(-12196.21, 62.5) * mm, "end": v(-12195.71, 62.5) * mm});
            skLineSegment(sketch, "E105.55.0.3", {"start": v(-12196.21, -62.5) * mm, "end": v(-12195.71, -62.5) * mm});
            skLineSegment(sketch, "E105.56.0.0", {"start": v(-12186.21, 62.5) * mm, "end": v(-12186.21, -62.5) * mm});
            skLineSegment(sketch, "E105.56.0.1", {"start": v(-12185.71, 62.5) * mm, "end": v(-12185.71, -62.5) * mm});
            skLineSegment(sketch, "E105.56.0.2", {"start": v(-12186.21, 62.5) * mm, "end": v(-12185.71, 62.5) * mm});
            skLineSegment(sketch, "E105.56.0.3", {"start": v(-12186.21, -62.5) * mm, "end": v(-12185.71, -62.5) * mm});
            skLineSegment(sketch, "E105.57.0.0", {"start": v(-12176.21, 62.5) * mm, "end": v(-12176.21, -62.5) * mm});
            skLineSegment(sketch, "E105.57.0.1", {"start": v(-12175.71, 62.5) * mm, "end": v(-12175.71, -62.5) * mm});
            skLineSegment(sketch, "E105.57.0.2", {"start": v(-12176.21, 62.5) * mm, "end": v(-12175.71, 62.5) * mm});
            skLineSegment(sketch, "E105.57.0.3", {"start": v(-12176.21, -62.5) * mm, "end": v(-12175.71, -62.5) * mm});
            skLineSegment(sketch, "E105.58.0.0", {"start": v(-12166.21, 62.5) * mm, "end": v(-12166.21, -62.5) * mm});
            skLineSegment(sketch, "E105.58.0.1", {"start": v(-12165.71, 62.5) * mm, "end": v(-12165.71, -62.5) * mm});
            skLineSegment(sketch, "E105.58.0.2", {"start": v(-12166.21, 62.5) * mm, "end": v(-12165.71, 62.5) * mm});
            skLineSegment(sketch, "E105.58.0.3", {"start": v(-12166.21, -62.5) * mm, "end": v(-12165.71, -62.5) * mm});
            skLineSegment(sketch, "E105.59.0.0", {"start": v(-12156.21, 62.5) * mm, "end": v(-12156.21, -62.5) * mm});
            skLineSegment(sketch, "E105.59.0.1", {"start": v(-12155.71, 62.5) * mm, "end": v(-12155.71, -62.5) * mm});
            skLineSegment(sketch, "E105.59.0.2", {"start": v(-12156.21, 62.5) * mm, "end": v(-12155.71, 62.5) * mm});
            skLineSegment(sketch, "E105.59.0.3", {"start": v(-12156.21, -62.5) * mm, "end": v(-12155.71, -62.5) * mm});
            skLineSegment(sketch, "E105.60.0.0", {"start": v(-12146.21, 62.5) * mm, "end": v(-12146.21, -62.5) * mm});
            skLineSegment(sketch, "E105.60.0.1", {"start": v(-12145.71, 62.5) * mm, "end": v(-12145.71, -62.5) * mm});
            skLineSegment(sketch, "E105.60.0.2", {"start": v(-12146.21, 62.5) * mm, "end": v(-12145.71, 62.5) * mm});
            skLineSegment(sketch, "E105.60.0.3", {"start": v(-12146.21, -62.5) * mm, "end": v(-12145.71, -62.5) * mm});
            skLineSegment(sketch, "E105.61.0.0", {"start": v(-12136.21, 62.5) * mm, "end": v(-12136.21, -62.5) * mm});
            skLineSegment(sketch, "E105.61.0.1", {"start": v(-12135.71, 62.5) * mm, "end": v(-12135.71, -62.5) * mm});
            skLineSegment(sketch, "E105.61.0.2", {"start": v(-12136.21, 62.5) * mm, "end": v(-12135.71, 62.5) * mm});
            skLineSegment(sketch, "E105.61.0.3", {"start": v(-12136.21, -62.5) * mm, "end": v(-12135.71, -62.5) * mm});
            skLineSegment(sketch, "E105.62.0.0", {"start": v(-12126.21, 62.5) * mm, "end": v(-12126.21, -62.5) * mm});
            skLineSegment(sketch, "E105.62.0.1", {"start": v(-12125.71, 62.5) * mm, "end": v(-12125.71, -62.5) * mm});
            skLineSegment(sketch, "E105.62.0.2", {"start": v(-12126.21, 62.5) * mm, "end": v(-12125.71, 62.5) * mm});
            skLineSegment(sketch, "E105.62.0.3", {"start": v(-12126.21, -62.5) * mm, "end": v(-12125.71, -62.5) * mm});
            skLineSegment(sketch, "E105.63.0.0", {"start": v(-12116.21, 62.5) * mm, "end": v(-12116.21, -62.5) * mm});
            skLineSegment(sketch, "E105.63.0.1", {"start": v(-12115.71, 62.5) * mm, "end": v(-12115.71, -62.5) * mm});
            skLineSegment(sketch, "E105.63.0.2", {"start": v(-12116.21, 62.5) * mm, "end": v(-12115.71, 62.5) * mm});
            skLineSegment(sketch, "E105.63.0.3", {"start": v(-12116.21, -62.5) * mm, "end": v(-12115.71, -62.5) * mm});
            skLineSegment(sketch, "E105.64.0.0", {"start": v(-12106.21, 62.5) * mm, "end": v(-12106.21, -62.5) * mm});
            skLineSegment(sketch, "E105.64.0.1", {"start": v(-12105.71, 62.5) * mm, "end": v(-12105.71, -62.5) * mm});
            skLineSegment(sketch, "E105.64.0.2", {"start": v(-12106.21, 62.5) * mm, "end": v(-12105.71, 62.5) * mm});
            skLineSegment(sketch, "E105.64.0.3", {"start": v(-12106.21, -62.5) * mm, "end": v(-12105.71, -62.5) * mm});
            skLineSegment(sketch, "E105.65.0.0", {"start": v(-12096.21, 62.5) * mm, "end": v(-12096.21, -62.5) * mm});
            skLineSegment(sketch, "E105.65.0.1", {"start": v(-12095.71, 62.5) * mm, "end": v(-12095.71, -62.5) * mm});
            skLineSegment(sketch, "E105.65.0.2", {"start": v(-12096.21, 62.5) * mm, "end": v(-12095.71, 62.5) * mm});
            skLineSegment(sketch, "E105.65.0.3", {"start": v(-12096.21, -62.5) * mm, "end": v(-12095.71, -62.5) * mm});
            skLineSegment(sketch, "E105.direction1", {"start": v(-12746.21, -62.5) * mm, "end": v(-12736.21, -62.5) * mm, "construction": true});
            skSolve(sketch);
        }
        {
            var Q0;
            Q0 = qSketchRegion(id + "F95", true);
            extrude(context, id + "F96", {"entities" : qUnion([Q0]), "operationType" : NewBodyOperationType.REMOVE, "oppositeDirection" : true, "depth" : 140 * mm});
        }
        {
            var Q0;
            Q0=makeQuery(id+"F52.opExtrude","SWEPT_FACE",FACE,{"disambiguationData":[OSD([sQuery(id+"F51.wireOp",EDGE,"E50.bottom")])]});
            var sketch = newSketch(context, id + "F97", { "sketchPlane" : qUnion([Q0])});
            skLineSegment(sketch, "E106.bottom", {"start": v(-4499.44, 18) * mm, "end": v(-3799.44, 18) * mm});
            skLineSegment(sketch, "E106.top", {"start": v(-4499.44, 16) * mm, "end": v(-3799.44, 16) * mm});
            skLineSegment(sketch, "E106.left", {"start": v(-4499.44, 18) * mm, "end": v(-4499.44, 16) * mm});
            skLineSegment(sketch, "E106.right", {"start": v(-3799.44, 18) * mm, "end": v(-3799.44, 16) * mm});
            skLineSegment(sketch, "E107.0.1.0", {"start": v(-4499.44, 14) * mm, "end": v(-4499.44, 12) * mm});
            skLineSegment(sketch, "E107.0.1.1", {"start": v(-4499.44, 14) * mm, "end": v(-3799.44, 14) * mm});
            skLineSegment(sketch, "E107.0.1.2", {"start": v(-4499.44, 12) * mm, "end": v(-3799.44, 12) * mm});
            skLineSegment(sketch, "E107.0.1.3", {"start": v(-3799.44, 14) * mm, "end": v(-3799.44, 12) * mm});
            skLineSegment(sketch, "E107.0.2.0", {"start": v(-4499.44, 10) * mm, "end": v(-4499.44, 8) * mm});
            skLineSegment(sketch, "E107.0.2.1", {"start": v(-4499.44, 10) * mm, "end": v(-3799.44, 10) * mm});
            skLineSegment(sketch, "E107.0.2.2", {"start": v(-4499.44, 8) * mm, "end": v(-3799.44, 8) * mm});
            skLineSegment(sketch, "E107.0.2.3", {"start": v(-3799.44, 10) * mm, "end": v(-3799.44, 8) * mm});
            skLineSegment(sketch, "E107.0.3.0", {"start": v(-4499.44, 6) * mm, "end": v(-4499.44, 4) * mm});
            skLineSegment(sketch, "E107.0.3.1", {"start": v(-4499.44, 6) * mm, "end": v(-3799.44, 6) * mm});
            skLineSegment(sketch, "E107.0.3.2", {"start": v(-4499.44, 4) * mm, "end": v(-3799.44, 4) * mm});
            skLineSegment(sketch, "E107.0.3.3", {"start": v(-3799.44, 6) * mm, "end": v(-3799.44, 4) * mm});
            skLineSegment(sketch, "E107.0.4.0", {"start": v(-4499.44, 2) * mm, "end": v(-4499.44, 0) * mm});
            skLineSegment(sketch, "E107.0.4.1", {"start": v(-4499.44, 2) * mm, "end": v(-3799.44, 2) * mm});
            skLineSegment(sketch, "E107.0.4.2", {"start": v(-4499.44, 0) * mm, "end": v(-3799.44, 0) * mm});
            skLineSegment(sketch, "E107.0.4.3", {"start": v(-3799.44, 2) * mm, "end": v(-3799.44, 0) * mm});
            skLineSegment(sketch, "E107.direction1", {"start": v(-4499.44, 16) * mm, "end": v(-4474.44, 16) * mm, "construction": true});
            skLineSegment(sketch, "E107.direction2", {"start": v(-4499.44, 16) * mm, "end": v(-4499.44, 12) * mm, "construction": true});
            skSolve(sketch);
        }
        {
            var Q0;
            Q0 = qSketchRegion(id + "F97", true);
            extrude(context, id + "F98", {"entities" : qUnion([Q0]), "operationType" : NewBodyOperationType.REMOVE, "oppositeDirection" : true, "depth" : 0.1 * mm});
        }
        {
            var Q0;
            Q0=makeQuery(id+"F52.opExtrude","SWEPT_FACE",FACE,{"disambiguationData":[OSD([sQuery(id+"F51.wireOp",EDGE,"E50.left")])]});
            var sketch = newSketch(context, id + "F99", { "sketchPlane" : qUnion([Q0])});
            skLineSegment(sketch, "E108.bottom", {"start": v(-225, 16) * mm, "end": v(225, 16) * mm});
            skLineSegment(sketch, "E108.top", {"start": v(-225, 18) * mm, "end": v(225, 18) * mm});
            skLineSegment(sketch, "E108.left", {"start": v(-225, 16) * mm, "end": v(-225, 18) * mm});
            skLineSegment(sketch, "E108.right", {"start": v(225, 16) * mm, "end": v(225, 18) * mm});
            skLineSegment(sketch, "E109.0.1.0", {"start": v(-225, 14) * mm, "end": v(225, 14) * mm});
            skLineSegment(sketch, "E109.0.1.1", {"start": v(-225, 12) * mm, "end": v(-225, 14) * mm});
            skLineSegment(sketch, "E109.0.1.2", {"start": v(-225, 12) * mm, "end": v(225, 12) * mm});
            skLineSegment(sketch, "E109.0.1.3", {"start": v(225, 12) * mm, "end": v(225, 14) * mm});
            skLineSegment(sketch, "E109.0.2.0", {"start": v(-225, 10) * mm, "end": v(225, 10) * mm});
            skLineSegment(sketch, "E109.0.2.1", {"start": v(-225, 8) * mm, "end": v(-225, 10) * mm});
            skLineSegment(sketch, "E109.0.2.2", {"start": v(-225, 8) * mm, "end": v(225, 8) * mm});
            skLineSegment(sketch, "E109.0.2.3", {"start": v(225, 8) * mm, "end": v(225, 10) * mm});
            skLineSegment(sketch, "E109.0.3.0", {"start": v(-225, 6) * mm, "end": v(225, 6) * mm});
            skLineSegment(sketch, "E109.0.3.1", {"start": v(-225, 4) * mm, "end": v(-225, 6) * mm});
            skLineSegment(sketch, "E109.0.3.2", {"start": v(-225, 4) * mm, "end": v(225, 4) * mm});
            skLineSegment(sketch, "E109.0.3.3", {"start": v(225, 4) * mm, "end": v(225, 6) * mm});
            skLineSegment(sketch, "E109.0.4.0", {"start": v(-225, 2) * mm, "end": v(225, 2) * mm});
            skLineSegment(sketch, "E109.0.4.1", {"start": v(-225, 0) * mm, "end": v(-225, 2) * mm});
            skLineSegment(sketch, "E109.0.4.2", {"start": v(-225, 0) * mm, "end": v(225, 0) * mm});
            skLineSegment(sketch, "E109.0.4.3", {"start": v(225, 0) * mm, "end": v(225, 2) * mm});
            skLineSegment(sketch, "E109.direction1", {"start": v(-225, 18) * mm, "end": v(-200, 18) * mm, "construction": true});
            skLineSegment(sketch, "E109.direction2", {"start": v(-225, 18) * mm, "end": v(-225, 14) * mm, "construction": true});
            skSolve(sketch);
        }
        {
            var Q0;
            Q0 = qSketchRegion(id + "F99", true);
            var Q1;
            Q1 = qConstructionFilter(qBodyType(qCreatedBy(id + "F99" ,EDGE), BodyType.WIRE), ConstructionObject.NO);
            extrude(context, id + "F100", {"entities" : qUnion([Q0]), "operationType" : NewBodyOperationType.REMOVE, "surfaceEntities" : qUnion([Q1]), "oppositeDirection" : true, "depth" : 0.1 * mm});
        }
        {
            var Q0;
            Q0=makeQuery(id+"F52.opExtrude","SWEPT_FACE",FACE,{"disambiguationData":[OSD([sQuery(id+"F51.wireOp",EDGE,"E50.right")])]});
            var sketch = newSketch(context, id + "F101", { "sketchPlane" : qUnion([Q0])});
            skLineSegment(sketch, "E110.bottom", {"start": v(-225, 18) * mm, "end": v(225, 18) * mm});
            skLineSegment(sketch, "E110.top", {"start": v(-225, 16) * mm, "end": v(225, 16) * mm});
            skLineSegment(sketch, "E110.left", {"start": v(-225, 18) * mm, "end": v(-225, 16) * mm});
            skLineSegment(sketch, "E110.right", {"start": v(225, 18) * mm, "end": v(225, 16) * mm});
            skLineSegment(sketch, "E111.0.1.0", {"start": v(-225, 14) * mm, "end": v(225, 14) * mm});
            skLineSegment(sketch, "E111.0.1.1", {"start": v(-225, 14) * mm, "end": v(-225, 12) * mm});
            skLineSegment(sketch, "E111.0.1.2", {"start": v(-225, 12) * mm, "end": v(225, 12) * mm});
            skLineSegment(sketch, "E111.0.1.3", {"start": v(225, 14) * mm, "end": v(225, 12) * mm});
            skLineSegment(sketch, "E111.0.2.0", {"start": v(-225, 10) * mm, "end": v(225, 10) * mm});
            skLineSegment(sketch, "E111.0.2.1", {"start": v(-225, 10) * mm, "end": v(-225, 8) * mm});
            skLineSegment(sketch, "E111.0.2.2", {"start": v(-225, 8) * mm, "end": v(225, 8) * mm});
            skLineSegment(sketch, "E111.0.2.3", {"start": v(225, 10) * mm, "end": v(225, 8) * mm});
            skLineSegment(sketch, "E111.0.3.0", {"start": v(-225, 6) * mm, "end": v(225, 6) * mm});
            skLineSegment(sketch, "E111.0.3.1", {"start": v(-225, 6) * mm, "end": v(-225, 4) * mm});
            skLineSegment(sketch, "E111.0.3.2", {"start": v(-225, 4) * mm, "end": v(225, 4) * mm});
            skLineSegment(sketch, "E111.0.3.3", {"start": v(225, 6) * mm, "end": v(225, 4) * mm});
            skLineSegment(sketch, "E111.0.4.0", {"start": v(-225, 2) * mm, "end": v(225, 2) * mm});
            skLineSegment(sketch, "E111.0.4.1", {"start": v(-225, 2) * mm, "end": v(-225, 0) * mm});
            skLineSegment(sketch, "E111.0.4.2", {"start": v(-225, 0) * mm, "end": v(225, 0) * mm});
            skLineSegment(sketch, "E111.0.4.3", {"start": v(225, 2) * mm, "end": v(225, 0) * mm});
            skLineSegment(sketch, "E111.direction1", {"start": v(-225, 18) * mm, "end": v(-200, 18) * mm, "construction": true});
            skLineSegment(sketch, "E111.direction2", {"start": v(-225, 18) * mm, "end": v(-225, 14) * mm, "construction": true});
            skSolve(sketch);
        }
        {
            var Q0;
            Q0 = qSketchRegion(id + "F101", true);
            extrude(context, id + "F102", {"entities" : qUnion([Q0]), "operationType" : NewBodyOperationType.REMOVE, "oppositeDirection" : true, "depth" : 0.1 * mm});
        }
        {
            var Q0;
            Q0=makeQuery(id+"F52.opExtrude","SWEPT_FACE",FACE,{"disambiguationData":[OSD([sQuery(id+"F51.wireOp",EDGE,"E50.top")])]});
            var sketch = newSketch(context, id + "F103", { "sketchPlane" : qUnion([Q0])});
            skLineSegment(sketch, "E112.bottom", {"start": v(4499.44, 18) * mm, "end": v(3799.44, 18) * mm});
            skLineSegment(sketch, "E112.top", {"start": v(4499.44, 16) * mm, "end": v(3799.44, 16) * mm});
            skLineSegment(sketch, "E112.left", {"start": v(4499.44, 18) * mm, "end": v(4499.44, 16) * mm});
            skLineSegment(sketch, "E112.right", {"start": v(3799.44, 18) * mm, "end": v(3799.44, 16) * mm});
            skLineSegment(sketch, "E113.0.1.0", {"start": v(4499.44, 14) * mm, "end": v(3799.44, 14) * mm});
            skLineSegment(sketch, "E113.0.1.1", {"start": v(3799.44, 14) * mm, "end": v(3799.44, 12) * mm});
            skLineSegment(sketch, "E113.0.1.2", {"start": v(4499.44, 12) * mm, "end": v(3799.44, 12) * mm});
            skLineSegment(sketch, "E113.0.1.3", {"start": v(4499.44, 14) * mm, "end": v(4499.44, 12) * mm});
            skLineSegment(sketch, "E113.0.2.0", {"start": v(4499.44, 10) * mm, "end": v(3799.44, 10) * mm});
            skLineSegment(sketch, "E113.0.2.1", {"start": v(3799.44, 10) * mm, "end": v(3799.44, 8) * mm});
            skLineSegment(sketch, "E113.0.2.2", {"start": v(4499.44, 8) * mm, "end": v(3799.44, 8) * mm});
            skLineSegment(sketch, "E113.0.2.3", {"start": v(4499.44, 10) * mm, "end": v(4499.44, 8) * mm});
            skLineSegment(sketch, "E113.0.3.0", {"start": v(4499.44, 6) * mm, "end": v(3799.44, 6) * mm});
            skLineSegment(sketch, "E113.0.3.1", {"start": v(3799.44, 6) * mm, "end": v(3799.44, 4) * mm});
            skLineSegment(sketch, "E113.0.3.2", {"start": v(4499.44, 4) * mm, "end": v(3799.44, 4) * mm});
            skLineSegment(sketch, "E113.0.3.3", {"start": v(4499.44, 6) * mm, "end": v(4499.44, 4) * mm});
            skLineSegment(sketch, "E113.0.4.0", {"start": v(4499.44, 2) * mm, "end": v(3799.44, 2) * mm});
            skLineSegment(sketch, "E113.0.4.1", {"start": v(3799.44, 2) * mm, "end": v(3799.44, 0) * mm});
            skLineSegment(sketch, "E113.0.4.2", {"start": v(4499.44, 0) * mm, "end": v(3799.44, 0) * mm});
            skLineSegment(sketch, "E113.0.4.3", {"start": v(4499.44, 2) * mm, "end": v(4499.44, 0) * mm});
            skLineSegment(sketch, "E113.direction1", {"start": v(3799.44, 18) * mm, "end": v(3824.44, 18) * mm, "construction": true});
            skLineSegment(sketch, "E113.direction2", {"start": v(3799.44, 18) * mm, "end": v(3799.44, 14) * mm, "construction": true});
            skSolve(sketch);
        }
        {
            var Q0;
            Q0 = qSketchRegion(id + "F103", true);
            extrude(context, id + "F104", {"entities" : qUnion([Q0]), "operationType" : NewBodyOperationType.REMOVE, "oppositeDirection" : true, "depth" : 0.1 * mm});
        }
    });
